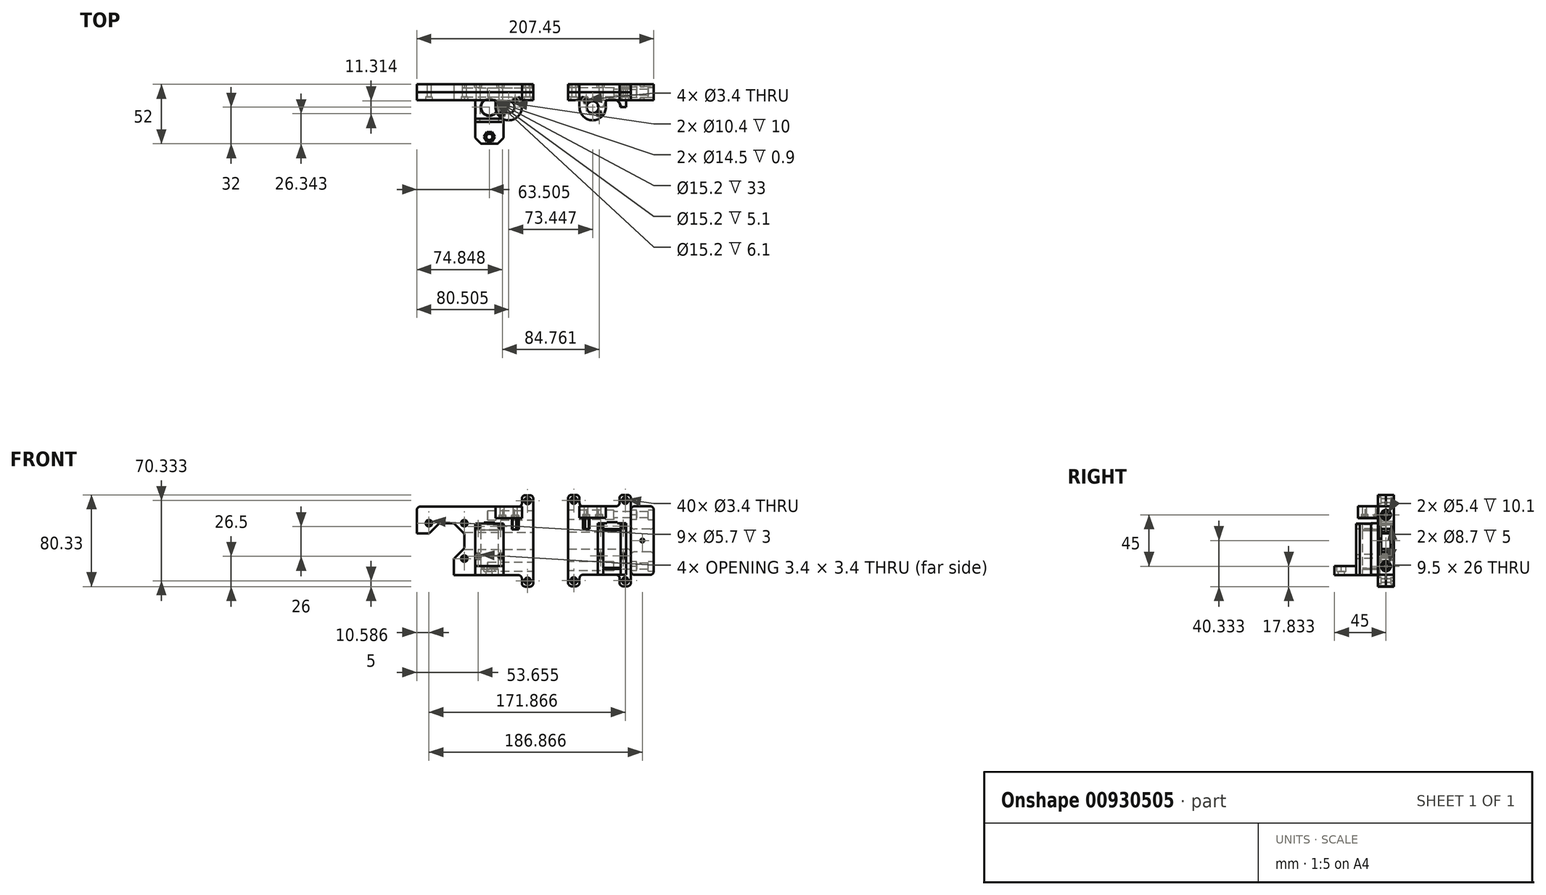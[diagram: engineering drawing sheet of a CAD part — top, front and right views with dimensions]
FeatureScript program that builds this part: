
annotation { "Feature Type Name" : "Feature", "Feature Type Description" : "" }
export const myFeature = defineFeature(function(context is Context, id is Id, definition is map)
    precondition{}
    {
        {
            assignVariable(context, id + "F0", {"name" : "Tolerance", "anyValue" : 0.2 * mm});
        }
        {
            assignVariable(context, id + "F1", {"name" : "RodHoleDepth", "anyValue" : 40 * mm});
        }
        {
            assignVariable(context, id + "F2", {"name" : "M3HeadRecessDepth", "anyValue" : 3 * mm});
        }
        {
            assignVariable(context, id + "F3", {"name" : "M3HexNutDepth", "anyValue" : 2.4 * mm + getVariable(context, 'Tolerance')});
        }
        {
            assignVariable(context, id + "F4", {"name" : "M5HeadRecessDepth", "anyValue" : 5 * mm});
        }
        {
            assignVariable(context, id + "F5", {"name" : "M5HoleDiameter", "anyValue" : 5.2 * mm + getVariable(context, 'Tolerance')});
        }
        {
            assignVariable(context, id + "F6", {"name" : "M5HexNutDepth", "anyValue" : 4.7 * mm + getVariable(context, 'Tolerance')});
        }
        {
            assignVariable(context, id + "F7", {"name" : "FilletRadius", "anyValue" : 3 * mm});
        }
        {
            var Q0;
            Q0=qCreatedBy(makeId("Front.planeOp"),FACE);
            var sketch = newSketch(context, id + "F8", { "sketchPlane" : qUnion([Q0])});
            skLineSegment(sketch, "E0", {"start": v(-115.9, 20) * mm, "end": v(-23.9, 20) * mm});
            skLineSegment(sketch, "E1", {"start": v(-23.9, 20) * mm, "end": v(-23.9, 10) * mm});
            skLineSegment(sketch, "E2", {"start": v(-115.9, 20) * mm, "end": v(-115.9, 80) * mm});
            skLineSegment(sketch, "E3", {"start": v(-115.9, 80) * mm, "end": v(-23.9, 80) * mm});
            skLineSegment(sketch, "E4", {"start": v(-23.9, 80) * mm, "end": v(-23.9, 90) * mm});
            skLineSegment(sketch, "E5", {"start": v(-13.9, 80) * mm, "end": v(-13.9, 20) * mm});
            skLineSegment(sketch, "E6", {"start": v(-13.9, 80) * mm, "end": v(-13.9, 90) * mm});
            skLineSegment(sketch, "E7", {"start": v(-13.9, 20) * mm, "end": v(-13.9, 10) * mm});
            skLineSegment(sketch, "E8", {"start": v(-23.9, 20) * mm, "end": v(-13.9, 20) * mm});
            skLineSegment(sketch, "E9", {"start": v(-23.9, 80) * mm, "end": v(-13.9, 80) * mm});
            skLineSegment(sketch, "E10", {"start": v(-13.9, 90) * mm, "end": v(-23.9, 90) * mm});
            skLineSegment(sketch, "E11", {"start": v(-13.9, 10) * mm, "end": v(-23.9, 10) * mm});
            skSolve(sketch);
        }
        {
            var Q0;
            Q0 = qSketchRegion(id + "F8", true);
            extrude(context, id + "F9", {"entities" : qUnion([Q0]), "oppositeDirection" : true, "depth" : 7 * mm, "offsetDistance" : 25 * mm});
        }
        {
            var Q0;
            Q0 = qSketchRegion(id + "F8", true);
            extrude(context, id + "F10", {"entities" : qUnion([Q0]), "depth" : 7 * mm, "offsetDistance" : 25 * mm});
        }
        {
            var Q0;
            Q0=makeQuery(id+"F10.opExtrude","CAP_FACE",FACE,{"disambiguationData":[OSD([sQuery(id+"F8.wireOp",EDGE,"E0"),sQuery(id+"F8.wireOp",EDGE,"E1"),sQuery(id+"F8.wireOp",EDGE,"4ElTsRrF-d6Ta-Xpu3-N1rJ-FU14qHi0ozwZ"),sQuery(id+"F8.wireOp",EDGE,"7PxteJ0w-hNWy-X14L-V5LG-c6Ao6gPeCcrO"),sQuery(id+"F8.wireOp",EDGE,"Jx2hsfEg-rsGK-g6mN-gGwm-UTiYR1x8r5xO"),sQuery(id+"F8.wireOp",EDGE,"E2"),sQuery(id+"F8.wireOp",EDGE,"E3"),sQuery(id+"F8.wireOp",EDGE,"E4"),sQuery(id+"F8.wireOp",EDGE,"orgWuDI4-4pWB-4aS4-cs57-z0Hx2wF69UBw"),sQuery(id+"F8.wireOp",EDGE,"4i0MoKHX-XmxI-cSmD-P7XZ-JZizBw6dTzRK"),sQuery(id+"F8.wireOp",EDGE,"mOqyP8SL-vEXn-Shjf-BXRA-A4QvbKXMYqA2"),sQuery(id+"F8.wireOp",EDGE,"E5")])],"isStart":false});
            var sketch = newSketch(context, id + "F11", { "sketchPlane" : qUnion([Q0])});
            skCircle(sketch, "E12.cCircle", {"center": v(-89.82, 50) * mm, "radius": 15.5 * mm, "construction": true});
            skLineSegment(sketch, "E12.0", {"start": v(-96.25, 65.5) * mm, "end": v(-83.4, 65.5) * mm});
            skLineSegment(sketch, "E12.1", {"start": v(-83.4, 65.5) * mm, "end": v(-74.32, 56.42) * mm});
            skLineSegment(sketch, "E12.2", {"start": v(-74.32, 56.42) * mm, "end": v(-74.32, 43.58) * mm});
            skLineSegment(sketch, "E12.3", {"start": v(-74.32, 43.58) * mm, "end": v(-83.4, 34.5) * mm});
            skLineSegment(sketch, "E12.7", {"start": v(-105.33, 56.42) * mm, "end": v(-96.25, 65.5) * mm});
            skPoint(sketch, "E12.0.midPoint", {"position": v(-89.82, 65.5) * mm});
            skLineSegment(sketch, "E13", {"start": v(-83.4, 34.5) * mm, "end": v(-83.4, 20) * mm});
            skLineSegment(sketch, "E14", {"start": v(-83.4, 20) * mm, "end": v(-115.9, 20) * mm});
            skLineSegment(sketch, "E15", {"start": v(-105.33, 56.42) * mm, "end": v(-115.9, 56.42) * mm});
            skLineSegment(sketch, "E16", {"start": v(-115.9, 56.42) * mm, "end": v(-115.9, 20) * mm});
            skSolve(sketch);
        }
        {
            var Q0;
            Q0 = qSketchRegion(id + "F11", true);
            extrude(context, id + "F12", {"entities" : qUnion([Q0]), "operationType" : NewBodyOperationType.REMOVE, "oppositeDirection" : true, "depth" : 25 * mm, "offsetDistance" : 25 * mm});
        }
        {
            var Q0;
            Q0=makeQuery(id+"F10.opExtrude","CAP_FACE",FACE,{"disambiguationData":[OSD([sQuery(id+"F8.wireOp",EDGE,"E0"),sQuery(id+"F8.wireOp",EDGE,"E1"),sQuery(id+"F8.wireOp",EDGE,"4ElTsRrF-d6Ta-Xpu3-N1rJ-FU14qHi0ozwZ"),sQuery(id+"F8.wireOp",EDGE,"7PxteJ0w-hNWy-X14L-V5LG-c6Ao6gPeCcrO"),sQuery(id+"F8.wireOp",EDGE,"Jx2hsfEg-rsGK-g6mN-gGwm-UTiYR1x8r5xO"),sQuery(id+"F8.wireOp",EDGE,"E2"),sQuery(id+"F8.wireOp",EDGE,"E3"),sQuery(id+"F8.wireOp",EDGE,"E4"),sQuery(id+"F8.wireOp",EDGE,"orgWuDI4-4pWB-4aS4-cs57-z0Hx2wF69UBw"),sQuery(id+"F8.wireOp",EDGE,"4i0MoKHX-XmxI-cSmD-P7XZ-JZizBw6dTzRK"),sQuery(id+"F8.wireOp",EDGE,"mOqyP8SL-vEXn-Shjf-BXRA-A4QvbKXMYqA2"),sQuery(id+"F8.wireOp",EDGE,"E5")])],"isStart":false});
            var sketch = newSketch(context, id + "F13", { "sketchPlane" : qUnion([Q0])});
            skPoint(sketch, "E17", {"position": v(-74.32, 65.5) * mm});
            skPoint(sketch, "E18", {"position": v(-74.32, 34.5) * mm});
            skCircle(sketch, "E19", {"center": v(-105.32, 65.5) * mm, "radius": 1.7 * mm});
            skCircle(sketch, "E20", {"center": v(-74.32, 65.5) * mm, "radius": 1.7 * mm});
            skCircle(sketch, "E21", {"center": v(-74.32, 34.5) * mm, "radius": 1.7 * mm});
            skCircle(sketch, "E22", {"center": v(-18.9, 85) * mm, "radius": 1.7 * mm});
            skPoint(sketch, "E22.centerSnap0", {"position": v(-23.9, 85) * mm});
            skPoint(sketch, "E22.centerSnap1", {"position": v(-18.9, 90) * mm});
            skCircle(sketch, "E23", {"center": v(-18.9, 15) * mm, "radius": 1.7 * mm});
            skPoint(sketch, "E23.centerSnap0", {"position": v(-18.9, 10) * mm});
            skPoint(sketch, "E23.centerSnap1", {"position": v(-23.9, 15) * mm});
            skSolve(sketch);
        }
        {
            var Q0;
            Q0 = qSketchRegion(id + "F13", true);
            extrude(context, id + "F14", {"entities" : qUnion([Q0]), "operationType" : NewBodyOperationType.REMOVE, "oppositeDirection" : true, "depth" : 25 * mm, "offsetDistance" : 25 * mm});
        }
        {
            var Q0;
            Q0=makeQuery(id+"F10.opExtrude","SWEPT_FACE",FACE,{"disambiguationData":[OSD([sQuery(id+"F8.wireOp",EDGE,"E5")])]});
            var sketch = newSketch(context, id + "F15", { "sketchPlane" : qUnion([Q0])});
            skLineSegment(sketch, "E24.bottom", {"start": v(-4, 42.5) * mm, "end": v(4, 42.5) * mm});
            skLineSegment(sketch, "E24.top", {"start": v(-4, 57.5) * mm, "end": v(4, 57.5) * mm});
            skLineSegment(sketch, "E24.left", {"start": v(-4, 42.5) * mm, "end": v(-4, 57.5) * mm});
            skLineSegment(sketch, "E24.right", {"start": v(4, 42.5) * mm, "end": v(4, 57.5) * mm});
            skSolve(sketch);
        }
        {
            var Q0;
            Q0 = qSketchRegion(id + "F15", true);
            extrude(context, id + "F16", {"entities" : qUnion([Q0]), "operationType" : NewBodyOperationType.REMOVE, "oppositeDirection" : true, "depth" : 65 * mm, "offsetDistance" : 25 * mm});
        }
        {
            var Q0;
            Q0=makeQuery(id+"F9.opExtrude","SWEPT_FACE",FACE,{"disambiguationData":[OSD([sQuery(id+"F8.wireOp",EDGE,"E5")])]});
            var sketch = newSketch(context, id + "F17", { "sketchPlane" : qUnion([Q0])});
            skCircle(sketch, "E25", {"center": v(0, 72.5) * mm, "radius": 4.1 * mm});
            skCircle(sketch, "E26", {"center": v(0, 27.5) * mm, "radius": 4.1 * mm});
            skSolve(sketch);
        }
        {
            var Q0;
            Q0 = qSketchRegion(id + "F17", true);
            extrude(context, id + "F18", {"entities" : qUnion([Q0]), "operationType" : NewBodyOperationType.REMOVE, "oppositeDirection" : true, "depth" : (getVariable(context, 'RodHoleDepth')), "offsetDistance" : 25 * mm});
        }
        {
            var Q0;
            Q0=makeQuery(id+"F10.opExtrude","SWEPT_FACE",FACE,{"disambiguationData":[OSD([sQuery(id+"F8.wireOp",EDGE,"E3")])]});
            var sketch = newSketch(context, id + "F19", { "sketchPlane" : qUnion([Q0])});
            skPoint(sketch, "E27", {"position": v(-46.9, -7) * mm});
            skPoint(sketch, "E28", {"position": v(-23.9, -7) * mm});
            skPoint(sketch, "E29", {"position": v(-35.4, -7) * mm});
            skPoint(sketch, "E30", {"position": v(-35.4, -13) * mm});
            skCircle(sketch, "E31", {"center": v(-35.4, -13) * mm, "radius": 5.2 * mm});
            skPoint(sketch, "E32", {"position": v(-35.4, -24.5) * mm});
            skLineSegment(sketch, "E33", {"start": v(-46.9, -7) * mm, "end": v(-23.9, -7) * mm});
            skArc(sketch, "E34", {"start": v(-35.4, -24.5) * mm, "mid": v(-27.27, -21.13) * mm, "end": v(-23.9, -13) * mm});
            skArc(sketch, "E35", {"start": v(-35.4, -24.5) * mm, "mid": v(-43.54, -21.13) * mm, "end": v(-46.9, -13) * mm});
            skLineSegment(sketch, "E36", {"start": v(-23.9, -7) * mm, "end": v(-23.9, -13) * mm});
            skLineSegment(sketch, "E37", {"start": v(-46.9, -7) * mm, "end": v(-46.9, -13) * mm});
            skSolve(sketch);
        }
        {
            var Q0;
            Q0 = qSketchRegion(id + "F19", true);
            extrude(context, id + "F20", {"entities" : qUnion([Q0]), "operationType" : NewBodyOperationType.ADD, "oppositeDirection" : true, "depth" : 10 * mm, "offsetDistance" : 25 * mm});
        }
        {
            var Q0;
            Q0=makeQuery(id+"F20.boolean.opBoolean","MERGE",FACE,{"derivedFrom":[makeQuery(id+"F10.opExtrude","SWEPT_FACE",FACE,{"disambiguationData":[OSD([sQuery(id+"F8.wireOp",EDGE,"E3")])]}),makeQuery(id+"F20.opExtrude","CAP_FACE",FACE,{"disambiguationData":[OSD([sQuery(id+"F19.wireOp",EDGE,"E31"),sQuery(id+"F19.wireOp",EDGE,"E33"),sQuery(id+"F19.wireOp",EDGE,"E34"),sQuery(id+"F19.wireOp",EDGE,"E35"),sQuery(id+"F19.wireOp",EDGE,"E36"),sQuery(id+"F19.wireOp",EDGE,"E37")])],"isStart":true})]});
            var sketch = newSketch(context, id + "F21", { "sketchPlane" : qUnion([Q0])});
            skPoint(sketch, "E38", {"position": v(-35.4, -13) * mm});
            skLineSegment(sketch, "E39", {"start": v(-35.4, -13) * mm, "end": v(-35.4, -5) * mm});
            skLineSegment(sketch, "E40", {"start": v(-35.4, -13) * mm, "end": v(-29.75, -7.34) * mm});
            skLineSegment(sketch, "E41", {"start": v(-35.4, -13) * mm, "end": v(-29.75, -18.66) * mm});
            skLineSegment(sketch, "E42", {"start": v(-35.4, -13) * mm, "end": v(-41.06, -18.66) * mm});
            skLineSegment(sketch, "E43", {"start": v(-35.4, -13) * mm, "end": v(-41.06, -7.34) * mm});
            skCircle(sketch, "E44", {"center": v(-29.75, -7.34) * mm, "radius": 1.7 * mm});
            skCircle(sketch, "E45", {"center": v(-41.06, -18.66) * mm, "radius": 1.7 * mm});
            skSolve(sketch);
        }
        {
            var Q0;
            Q0 = qSketchRegion(id + "F21", true);
            extrude(context, id + "F22", {"entities" : qUnion([Q0]), "operationType" : NewBodyOperationType.REMOVE, "oppositeDirection" : true, "depth" : 12.5 * mm, "offsetDistance" : 25 * mm});
        }
        {
            var Q0;
            Q0=makeQuery(id+"F20.opExtrude","CAP_FACE",FACE,{"disambiguationData":[OSD([sQuery(id+"F19.wireOp",EDGE,"E31"),sQuery(id+"F19.wireOp",EDGE,"E33"),sQuery(id+"F19.wireOp",EDGE,"E34"),sQuery(id+"F19.wireOp",EDGE,"E35"),sQuery(id+"F19.wireOp",EDGE,"E36"),sQuery(id+"F19.wireOp",EDGE,"E37")])],"isStart":false});
            var sketch = newSketch(context, id + "F23", { "sketchPlane" : qUnion([Q0])});
            skPoint(sketch, "E46", {"position": v(-35.4, 13) * mm});
            skPoint(sketch, "E47", {"position": v(-41.06, 18.66) * mm});
            skPoint(sketch, "E48.positionSnap0", {"position": v(-29.75, 9.04) * mm});
            skLineSegment(sketch, "E49", {"start": v(-41.06, 18.66) * mm, "end": v(-35.4, 13) * mm});
            skLineSegment(sketch, "E50", {"start": v(-35.4, 13) * mm, "end": v(-29.75, 7.34) * mm});
            skCircle(sketch, "E51.cCircle", {"center": v(-41.06, 18.66) * mm, "radius": 2.8 * mm, "construction": true});
            skLineSegment(sketch, "E51.0", {"start": v(-37.94, 17.82) * mm, "end": v(-40.23, 15.53) * mm});
            skLineSegment(sketch, "E51.1", {"start": v(-40.23, 15.53) * mm, "end": v(-43.35, 16.37) * mm});
            skLineSegment(sketch, "E51.2", {"start": v(-43.35, 16.37) * mm, "end": v(-44.19, 19.5) * mm});
            skLineSegment(sketch, "E51.3", {"start": v(-44.19, 19.5) * mm, "end": v(-41.9, 21.78) * mm});
            skLineSegment(sketch, "E51.4", {"start": v(-41.9, 21.78) * mm, "end": v(-38.78, 20.94) * mm});
            skLineSegment(sketch, "E51.5", {"start": v(-38.78, 20.94) * mm, "end": v(-37.94, 17.82) * mm});
            skPoint(sketch, "E51.0.midPoint", {"position": v(-39.08, 16.68) * mm});
            skCircle(sketch, "E52.cCircle", {"center": v(-29.75, 7.34) * mm, "radius": 2.8 * mm, "construction": true});
            skLineSegment(sketch, "E52.0", {"start": v(-32.87, 8.18) * mm, "end": v(-30.59, 10.47) * mm});
            skLineSegment(sketch, "E52.1", {"start": v(-30.59, 10.47) * mm, "end": v(-27.46, 9.63) * mm});
            skLineSegment(sketch, "E52.2", {"start": v(-27.46, 9.63) * mm, "end": v(-26.63, 6.5) * mm});
            skLineSegment(sketch, "E52.3", {"start": v(-26.63, 6.5) * mm, "end": v(-28.91, 4.22) * mm});
            skLineSegment(sketch, "E52.4", {"start": v(-28.91, 4.22) * mm, "end": v(-32.03, 5.06) * mm});
            skLineSegment(sketch, "E52.5", {"start": v(-32.03, 5.06) * mm, "end": v(-32.87, 8.18) * mm});
            skPoint(sketch, "E52.0.midPoint", {"position": v(-31.73, 9.32) * mm});
            skLineSegment(sketch, "E53", {"start": v(-40.23, 15.53) * mm, "end": v(-39.26, 15.28) * mm});
            skLineSegment(sketch, "E54", {"start": v(-37.94, 17.82) * mm, "end": v(-37.68, 16.85) * mm});
            skLineSegment(sketch, "E55", {"start": v(-39.26, 15.28) * mm, "end": v(-37.68, 16.85) * mm});
            skLineSegment(sketch, "E56", {"start": v(-32.87, 8.18) * mm, "end": v(-33.13, 9.15) * mm});
            skLineSegment(sketch, "E57", {"start": v(-30.59, 10.47) * mm, "end": v(-31.55, 10.72) * mm});
            skLineSegment(sketch, "E58", {"start": v(-33.13, 9.15) * mm, "end": v(-31.55, 10.72) * mm});
            skSolve(sketch);
        }
        {
            var Q0;
            Q0 = qSketchRegion(id + "F23", true);
            extrude(context, id + "F24", {"entities" : qUnion([Q0]), "operationType" : NewBodyOperationType.REMOVE, "oppositeDirection" : true, "depth" : (getVariable(context, 'M3HexNutDepth')), "offsetDistance" : 25 * mm});
        }
        {
            var Q0;
            Q0 = qSketchRegion(id + "F23", true);
            extrude(context, id + "F25", {"entities" : qUnion([Q0]), "operationType" : NewBodyOperationType.REMOVE, "depth" : 10 * mm, "offsetDistance" : 25 * mm});
        }
        {
            var Q0;
            Q0=makeQuery(id+"F10.opExtrude","SWEPT_FACE",FACE,{"disambiguationData":[OSD([sQuery(id+"F8.wireOp",EDGE,"E0")])]});
            var sketch = newSketch(context, id + "F26", { "sketchPlane" : qUnion([Q0])});
            skPoint(sketch, "E59", {"position": v(-35.4, 7) * mm});
            skPoint(sketch, "E60", {"position": v(-52.4, 13) * mm});
            skArc(sketch, "E61", {"start": v(-44.8, 13) * mm, "mid": v(-52.4, 5.4) * mm, "end": v(-60, 13) * mm});
            skArc(sketch, "E62", {"start": v(-48.4, 13) * mm, "mid": v(-52.4, 9) * mm, "end": v(-56.4, 13) * mm});
            skLineSegment(sketch, "E63", {"start": v(-56.4, 13) * mm, "end": v(-60, 13) * mm});
            skLineSegment(sketch, "E64", {"start": v(-48.4, 13) * mm, "end": v(-44.8, 13) * mm});
            skPoint(sketch, "E65", {"position": v(-35.4, 13) * mm});
            skSolve(sketch);
        }
        {
            var Q0;
            Q0 = qSketchRegion(id + "F26", true);
            extrude(context, id + "F27", {"entities" : qUnion([Q0]), "operationType" : NewBodyOperationType.REMOVE, "oppositeDirection" : true, "depth" : 46 * mm, "offsetDistance" : 25 * mm});
        }
        {
            var Q0;
            Q0=makeQuery(id+"F10.opExtrude","SWEPT_FACE",FACE,{"disambiguationData":[OSD([sQuery(id+"F8.wireOp",EDGE,"E0")])]});
            var sketch = newSketch(context, id + "F28", { "sketchPlane" : qUnion([Q0])});
            skPoint(sketch, "E66", {"position": v(-52.4, 13) * mm});
            skArc(sketch, "E67", {"start": v(-60, 13) * mm, "mid": v(-52.4, 5.4) * mm, "end": v(-44.8, 13) * mm});
            skLineSegment(sketch, "E68", {"start": v(-44.8, 13) * mm, "end": v(-40.06, 13) * mm});
            skLineSegment(sketch, "E69", {"start": v(-60, 13) * mm, "end": v(-64.76, 13) * mm});
            skLineSegment(sketch, "E70", {"start": v(-40.06, 13) * mm, "end": v(-40.06, 7) * mm});
            skLineSegment(sketch, "E71", {"start": v(-40.06, 7) * mm, "end": v(-47.74, 7) * mm});
            skLineSegment(sketch, "E72", {"start": v(-64.76, 13) * mm, "end": v(-64.76, 7) * mm});
            skLineSegment(sketch, "E73", {"start": v(-64.76, 7) * mm, "end": v(-57.07, 7) * mm});
            skSolve(sketch);
        }
        {
            var Q0;
            Q0 = qSketchRegion(id + "F28", true);
            extrude(context, id + "F29", {"entities" : qUnion([Q0]), "operationType" : NewBodyOperationType.ADD, "oppositeDirection" : true, "depth" : (5 * mm + getVariable(context, 'Tolerance') / 2), "offsetDistance" : 25 * mm});
        }
        {
            var Q0;
            Q0=makeQuery(id+"F29.opExtrude","CAP_FACE",FACE,{"disambiguationData":[OSD([sQuery(id+"F28.wireOp",EDGE,"E67"),sQuery(id+"F28.wireOp",EDGE,"E68"),sQuery(id+"F28.wireOp",EDGE,"E70"),sQuery(id+"F28.wireOp",EDGE,"E71")])],"isStart":false});
            var sketch = newSketch(context, id + "F30", { "sketchPlane" : qUnion([Q0])});
            skPoint(sketch, "E74", {"position": v(-52.4, -13) * mm});
            skArc(sketch, "E75", {"start": v(-45.16, -13) * mm, "mid": v(-52.4, -5.75) * mm, "end": v(-59.66, -13) * mm});
            skLineSegment(sketch, "E76", {"start": v(-45.16, -13) * mm, "end": v(-40.06, -13) * mm});
            skLineSegment(sketch, "E77", {"start": v(-40.06, -13) * mm, "end": v(-40.06, -5) * mm});
            skLineSegment(sketch, "E78", {"start": v(-59.66, -13) * mm, "end": v(-64.76, -13) * mm});
            skLineSegment(sketch, "E79", {"start": v(-64.76, -13) * mm, "end": v(-64.76, -5) * mm});
            skLineSegment(sketch, "E80", {"start": v(-64.76, -5) * mm, "end": v(-40.06, -5) * mm});
            skSolve(sketch);
        }
        {
            var Q0;
            Q0 = qSketchRegion(id + "F30", true);
            extrude(context, id + "F31", {"entities" : qUnion([Q0]), "operationType" : NewBodyOperationType.ADD, "depth" : 1.1 * mm - getVariable(context, 'Tolerance'), "offsetDistance" : 25 * mm});
        }
        {
            var Q0;
            Q0=makeQuery(id+"F31.opExtrude","CAP_FACE",FACE,{"disambiguationData":[OSD([sQuery(id+"F30.wireOp",EDGE,"E75"),sQuery(id+"F30.wireOp",EDGE,"xVCJ5Ixd-oV9c-nEpF-QwK2-FCStSbNz6csr"),sQuery(id+"F30.wireOp",EDGE,"KKsrvb3y-Tanb-XRHW-Xvde-AmVJSpIleMcL"),sQuery(id+"F30.wireOp",EDGE,"jJWCP0GL-qmZ0-jQ3C-Ld0P-dRRUBaJsqygn"),sQuery(id+"F30.wireOp",EDGE,"l5prBngy-kXb7-NS8M-DBdE-vMuQnj67Dzb8"),sQuery(id+"F30.wireOp",EDGE,"qzUSBdcP-XdCP-zqGN-MzMA-phhTVpw7iq0O")])],"isStart":false});
            var sketch = newSketch(context, id + "F32", { "sketchPlane" : qUnion([Q0])});
            skPoint(sketch, "E81", {"position": v(-52.4, -13) * mm});
            skArc(sketch, "E82", {"start": v(-44.8, -13) * mm, "mid": v(-52.4, -5.4) * mm, "end": v(-60, -13) * mm});
            skLineSegment(sketch, "E83", {"start": v(-60, -13) * mm, "end": v(-64.76, -13) * mm});
            skLineSegment(sketch, "E84", {"start": v(-64.76, -13) * mm, "end": v(-64.76, -5) * mm});
            skLineSegment(sketch, "E85", {"start": v(-44.8, -13) * mm, "end": v(-40.06, -13) * mm});
            skLineSegment(sketch, "E86", {"start": v(-40.06, -13) * mm, "end": v(-40.06, -5) * mm});
            skLineSegment(sketch, "E87", {"start": v(-64.76, -5) * mm, "end": v(-40.06, -5) * mm});
            skSolve(sketch);
        }
        {
            var Q0;
            Q0 = qSketchRegion(id + "F32", true);
            extrude(context, id + "F33", {"entities" : qUnion([Q0]), "operationType" : NewBodyOperationType.ADD, "depth" : 32.8 * mm + getVariable(context, 'Tolerance'), "offsetDistance" : 25 * mm});
        }
        {
            var Q0;
            {var subQ0=sQuery(id+"F32.wireOp",EDGE,"u7j6INuo-gqj2-xr2Y-Kvyz-7sy1viPy3Nbp");var subQ1=sQuery(id+"F32.wireOp",EDGE,"E82");var subQ3=sQuery(id+"F28.wireOp",EDGE,"E69");var subQ4=sQuery(id+"F32.wireOp",EDGE,"uuo2rrgI-b8Mf-HUeX-D92I-OpvW8boPGIY9");Q0=makeQuery(id+"F33.boolean.opBoolean","SPLIT",FACE,{"disambiguationData":[TD([makeQuery(id+"F29.opExtrude","SWEPT_FACE",FACE,{"disambiguationData":[OSD([subQ3])]})])],"derivedFrom":makeQuery(id+"F33.opExtrude","CAP_FACE",FACE,{"disambiguationData":[OSD([subQ1,subQ0,sQuery(id+"F32.wireOp",EDGE,"ZIB3AkM0-OxwD-h3Ax-mLtj-ZQacNZoiAByL"),sQuery(id+"F32.wireOp",EDGE,"DisRxEdu-4dno-EZQz-xngY-1mmXhpX3mB9u"),subQ4,sQuery(id+"F32.wireOp",EDGE,"J3FYGhw3-x3kB-kLge-yOmn-sRuC37IefDrh")])],"isStart":false})});}
            var sketch = newSketch(context, id + "F34", { "sketchPlane" : qUnion([Q0])});
            skPoint(sketch, "E88", {"position": v(-52.4, -13) * mm});
            skArc(sketch, "E89", {"start": v(-45.16, -13) * mm, "mid": v(-52.4, -5.75) * mm, "end": v(-59.66, -13) * mm});
            skLineSegment(sketch, "E90", {"start": v(-59.66, -13) * mm, "end": v(-64.76, -13) * mm});
            skLineSegment(sketch, "E91", {"start": v(-45.16, -13) * mm, "end": v(-40.06, -13) * mm});
            skLineSegment(sketch, "E92", {"start": v(-40.06, -13) * mm, "end": v(-40.06, -5) * mm});
            skLineSegment(sketch, "E93", {"start": v(-64.76, -13) * mm, "end": v(-64.76, -5) * mm});
            skLineSegment(sketch, "E94", {"start": v(-64.76, -5) * mm, "end": v(-40.06, -5) * mm});
            skSolve(sketch);
        }
        {
            var Q0;
            Q0 = qSketchRegion(id + "F34", true);
            extrude(context, id + "F35", {"entities" : qUnion([Q0]), "operationType" : NewBodyOperationType.ADD, "depth" : 1.1 * mm - getVariable(context, 'Tolerance'), "offsetDistance" : 25 * mm});
        }
        {
            var Q0;
            Q0=makeQuery(id+"F35.opExtrude","CAP_FACE",FACE,{"disambiguationData":[OSD([sQuery(id+"F34.wireOp",EDGE,"E89"),sQuery(id+"F34.wireOp",EDGE,"GdwB4Kny-1C7h-vXFo-lqtw-lYCse3TfWah3"),sQuery(id+"F34.wireOp",EDGE,"UIoDu40C-p5wn-kfFw-dchT-OTPBX3CLgIoY"),sQuery(id+"F34.wireOp",EDGE,"nKK0WJDT-j9Y7-Eu8t-1ZP1-kCxPYY3NenT9"),sQuery(id+"F34.wireOp",EDGE,"1FnQ6s0P-5r0c-BRcY-ZU3t-i9w6pcUyLMfj"),sQuery(id+"F34.wireOp",EDGE,"748WQctB-3RJW-Xf6T-p68E-eUlEy1FFqQs4")])],"isStart":false});
            var sketch = newSketch(context, id + "F36", { "sketchPlane" : qUnion([Q0])});
            skPoint(sketch, "E95", {"position": v(-52.4, -13) * mm});
            skArc(sketch, "E96", {"start": v(-44.8, -13) * mm, "mid": v(-52.4, -5.4) * mm, "end": v(-60, -13) * mm});
            skLineSegment(sketch, "E97", {"start": v(-44.8, -13) * mm, "end": v(-40.06, -13) * mm});
            skLineSegment(sketch, "E98", {"start": v(-40.06, -13) * mm, "end": v(-40.06, -5) * mm});
            skLineSegment(sketch, "E99", {"start": v(-60, -13) * mm, "end": v(-64.76, -13) * mm});
            skLineSegment(sketch, "E100", {"start": v(-64.76, -13) * mm, "end": v(-64.76, -5) * mm});
            skLineSegment(sketch, "E101", {"start": v(-64.76, -5) * mm, "end": v(-40.06, -5) * mm});
            skSolve(sketch);
        }
        {
            var Q0;
            Q0 = qSketchRegion(id + "F36", true);
            extrude(context, id + "F37", {"entities" : qUnion([Q0]), "operationType" : NewBodyOperationType.ADD, "depth" : 5 * mm + (getVariable(context, 'Tolerance') / 2), "offsetDistance" : 25 * mm});
        }
        {
            var Q0;
            Q0=makeQuery(id+"F37.boolean.opBoolean","MERGE",FACE,{"derivedFrom":[makeQuery(id+"F35.boolean.opBoolean","MERGE",FACE,{"derivedFrom":[makeQuery(id+"F33.boolean.opBoolean","MERGE",FACE,{"derivedFrom":[makeQuery(id+"F31.boolean.opBoolean","MERGE",FACE,{"derivedFrom":[makeQuery(id+"F29.opExtrude","SWEPT_FACE",FACE,{"disambiguationData":[OSD([sQuery(id+"F28.wireOp",EDGE,"E69")])]}),makeQuery(id+"F31.opExtrude","SWEPT_FACE",FACE,{"disambiguationData":[OSD([sQuery(id+"F30.wireOp",EDGE,"xVCJ5Ixd-oV9c-nEpF-QwK2-FCStSbNz6csr")])]})]}),makeQuery(id+"F33.opExtrude","SWEPT_FACE",FACE,{"disambiguationData":[OSD([sQuery(id+"F32.wireOp",EDGE,"u7j6INuo-gqj2-xr2Y-Kvyz-7sy1viPy3Nbp")])]})]}),makeQuery(id+"F35.opExtrude","SWEPT_FACE",FACE,{"disambiguationData":[OSD([sQuery(id+"F34.wireOp",EDGE,"UIoDu40C-p5wn-kfFw-dchT-OTPBX3CLgIoY")])]})]}),makeQuery(id+"F37.opExtrude","SWEPT_FACE",FACE,{"disambiguationData":[OSD([sQuery(id+"F36.wireOp",EDGE,"6wegHLb0-SrSl-BNs0-chY1-SGuGLHtS43J8")])]})]});
            var sketch = newSketch(context, id + "F38", { "sketchPlane" : qUnion([Q0])});
            skPoint(sketch, "E102", {"position": v(-62.26, 62.5) * mm});
            skCircle(sketch, "E103", {"center": v(-62.26, 62.5) * mm, "radius": 1.7 * mm});
            skPoint(sketch, "E104", {"position": v(-62.26, 36.5) * mm});
            skPoint(sketch, "E105", {"position": v(-42.56, 62.5) * mm});
            skCircle(sketch, "E106", {"center": v(-42.56, 62.5) * mm, "radius": 1.7 * mm});
            skCircle(sketch, "E107", {"center": v(-62.26, 36.5) * mm, "radius": 1.7 * mm});
            skPoint(sketch, "E108", {"position": v(-42.56, 36.5) * mm});
            skCircle(sketch, "E109", {"center": v(-42.56, 36.5) * mm, "radius": 1.7 * mm});
            skSolve(sketch);
        }
        {
            var Q0;
            Q0 = qSketchRegion(id + "F38", true);
            extrude(context, id + "F39", {"entities" : qUnion([Q0]), "operationType" : NewBodyOperationType.REMOVE, "oppositeDirection" : true, "depth" : 20 * mm, "offsetDistance" : 25 * mm});
        }
        {
            var Q0;
            Q0=makeQuery(id+"F9.opExtrude","CAP_FACE",FACE,{"disambiguationData":[OSD([sQuery(id+"F8.wireOp",EDGE,"E0"),sQuery(id+"F8.wireOp",EDGE,"E1"),sQuery(id+"F8.wireOp",EDGE,"4ElTsRrF-d6Ta-Xpu3-N1rJ-FU14qHi0ozwZ"),sQuery(id+"F8.wireOp",EDGE,"7PxteJ0w-hNWy-X14L-V5LG-c6Ao6gPeCcrO"),sQuery(id+"F8.wireOp",EDGE,"Jx2hsfEg-rsGK-g6mN-gGwm-UTiYR1x8r5xO"),sQuery(id+"F8.wireOp",EDGE,"E2"),sQuery(id+"F8.wireOp",EDGE,"E3"),sQuery(id+"F8.wireOp",EDGE,"E4"),sQuery(id+"F8.wireOp",EDGE,"orgWuDI4-4pWB-4aS4-cs57-z0Hx2wF69UBw"),sQuery(id+"F8.wireOp",EDGE,"4i0MoKHX-XmxI-cSmD-P7XZ-JZizBw6dTzRK"),sQuery(id+"F8.wireOp",EDGE,"mOqyP8SL-vEXn-Shjf-BXRA-A4QvbKXMYqA2"),sQuery(id+"F8.wireOp",EDGE,"E5")])],"isStart":false});
            var sketch = newSketch(context, id + "F40", { "sketchPlane" : qUnion([Q0])});
            skCircle(sketch, "E110.cCircle", {"center": v(18.9, 85) * mm, "radius": 2.8 * mm, "construction": true});
            skLineSegment(sketch, "E110.0", {"start": v(17.29, 87.8) * mm, "end": v(20.52, 87.8) * mm});
            skLineSegment(sketch, "E110.1", {"start": v(20.52, 87.8) * mm, "end": v(22.14, 85) * mm});
            skLineSegment(sketch, "E110.2", {"start": v(22.14, 85) * mm, "end": v(20.52, 82.2) * mm});
            skLineSegment(sketch, "E110.3", {"start": v(20.52, 82.2) * mm, "end": v(17.29, 82.2) * mm});
            skLineSegment(sketch, "E110.4", {"start": v(17.29, 82.2) * mm, "end": v(15.67, 85) * mm});
            skLineSegment(sketch, "E110.5", {"start": v(15.67, 85) * mm, "end": v(17.29, 87.8) * mm});
            skPoint(sketch, "E110.0.midPoint", {"position": v(18.9, 87.8) * mm});
            skCircle(sketch, "E111.cCircle", {"center": v(18.9, 15) * mm, "radius": 2.8 * mm, "construction": true});
            skLineSegment(sketch, "E111.0", {"start": v(17.34, 17.83) * mm, "end": v(20.57, 17.77) * mm});
            skLineSegment(sketch, "E111.1", {"start": v(20.57, 17.77) * mm, "end": v(22.14, 14.95) * mm});
            skLineSegment(sketch, "E111.2", {"start": v(22.14, 14.95) * mm, "end": v(20.47, 12.17) * mm});
            skLineSegment(sketch, "E111.3", {"start": v(20.47, 12.17) * mm, "end": v(17.24, 12.23) * mm});
            skLineSegment(sketch, "E111.4", {"start": v(17.24, 12.23) * mm, "end": v(15.67, 15.05) * mm});
            skLineSegment(sketch, "E111.5", {"start": v(15.67, 15.05) * mm, "end": v(17.34, 17.83) * mm});
            skPoint(sketch, "E111.0.midPoint", {"position": v(18.95, 17.8) * mm});
            skCircle(sketch, "E112.cCircle", {"center": v(42.56, 62.5) * mm, "radius": 2.8 * mm, "construction": true});
            skLineSegment(sketch, "E112.0", {"start": v(40.94, 65.3) * mm, "end": v(44.17, 65.3) * mm});
            skLineSegment(sketch, "E112.1", {"start": v(44.17, 65.3) * mm, "end": v(45.79, 62.5) * mm});
            skLineSegment(sketch, "E112.2", {"start": v(45.79, 62.5) * mm, "end": v(44.17, 59.7) * mm});
            skLineSegment(sketch, "E112.3", {"start": v(44.17, 59.7) * mm, "end": v(40.94, 59.7) * mm});
            skLineSegment(sketch, "E112.4", {"start": v(40.94, 59.7) * mm, "end": v(39.32, 62.5) * mm});
            skLineSegment(sketch, "E112.5", {"start": v(39.32, 62.5) * mm, "end": v(40.94, 65.3) * mm});
            skPoint(sketch, "E112.0.midPoint", {"position": v(42.56, 65.3) * mm});
            skCircle(sketch, "E113.cCircle", {"center": v(62.26, 62.5) * mm, "radius": 2.8 * mm, "construction": true});
            skLineSegment(sketch, "E113.0", {"start": v(60.64, 65.3) * mm, "end": v(63.87, 65.3) * mm});
            skLineSegment(sketch, "E113.1", {"start": v(63.87, 65.3) * mm, "end": v(65.49, 62.5) * mm});
            skLineSegment(sketch, "E113.2", {"start": v(65.49, 62.5) * mm, "end": v(63.87, 59.7) * mm});
            skLineSegment(sketch, "E113.3", {"start": v(63.87, 59.7) * mm, "end": v(60.64, 59.7) * mm});
            skLineSegment(sketch, "E113.4", {"start": v(60.64, 59.7) * mm, "end": v(59.02, 62.5) * mm});
            skLineSegment(sketch, "E113.5", {"start": v(59.02, 62.5) * mm, "end": v(60.64, 65.3) * mm});
            skPoint(sketch, "E113.0.midPoint", {"position": v(62.26, 65.3) * mm});
            skCircle(sketch, "E114.cCircle", {"center": v(42.56, 36.5) * mm, "radius": 2.8 * mm, "construction": true});
            skLineSegment(sketch, "E114.0", {"start": v(40.94, 39.3) * mm, "end": v(44.17, 39.3) * mm});
            skLineSegment(sketch, "E114.1", {"start": v(44.17, 39.3) * mm, "end": v(45.79, 36.5) * mm});
            skLineSegment(sketch, "E114.2", {"start": v(45.79, 36.5) * mm, "end": v(44.17, 33.7) * mm});
            skLineSegment(sketch, "E114.3", {"start": v(44.17, 33.7) * mm, "end": v(40.94, 33.7) * mm});
            skLineSegment(sketch, "E114.4", {"start": v(40.94, 33.7) * mm, "end": v(39.32, 36.5) * mm});
            skLineSegment(sketch, "E114.5", {"start": v(39.32, 36.5) * mm, "end": v(40.94, 39.3) * mm});
            skPoint(sketch, "E114.0.midPoint", {"position": v(42.56, 39.3) * mm});
            skCircle(sketch, "E115.cCircle", {"center": v(62.26, 36.5) * mm, "radius": 2.8 * mm, "construction": true});
            skLineSegment(sketch, "E115.0", {"start": v(60.64, 39.3) * mm, "end": v(63.87, 39.3) * mm});
            skLineSegment(sketch, "E115.1", {"start": v(63.87, 39.3) * mm, "end": v(65.49, 36.5) * mm});
            skLineSegment(sketch, "E115.2", {"start": v(65.49, 36.5) * mm, "end": v(63.87, 33.7) * mm});
            skLineSegment(sketch, "E115.3", {"start": v(63.87, 33.7) * mm, "end": v(60.64, 33.7) * mm});
            skLineSegment(sketch, "E115.4", {"start": v(60.64, 33.7) * mm, "end": v(59.02, 36.5) * mm});
            skLineSegment(sketch, "E115.5", {"start": v(59.02, 36.5) * mm, "end": v(60.64, 39.3) * mm});
            skPoint(sketch, "E115.0.midPoint", {"position": v(62.26, 39.3) * mm});
            skSolve(sketch);
        }
        {
            var Q0;
            Q0 = qSketchRegion(id + "F40", true);
            extrude(context, id + "F41", {"entities" : qUnion([Q0]), "operationType" : NewBodyOperationType.REMOVE, "oppositeDirection" : true, "depth" : getVariable(context, 'M3HexNutDepth'), "offsetDistance" : 25 * mm});
        }
        {
            var Q0;
            {var subQ0=sQuery(id+"F8.wireOp",EDGE,"E5");var subQ1=sQuery(id+"F8.wireOp",EDGE,"mOqyP8SL-vEXn-Shjf-BXRA-A4QvbKXMYqA2");var subQ2=sQuery(id+"F8.wireOp",EDGE,"4i0MoKHX-XmxI-cSmD-P7XZ-JZizBw6dTzRK");var subQ3=sQuery(id+"F8.wireOp",EDGE,"orgWuDI4-4pWB-4aS4-cs57-z0Hx2wF69UBw");var subQ4=sQuery(id+"F8.wireOp",EDGE,"E4");var subQ5=sQuery(id+"F8.wireOp",EDGE,"E3");var subQ6=sQuery(id+"F8.wireOp",EDGE,"E2");var subQ7=sQuery(id+"F8.wireOp",EDGE,"Jx2hsfEg-rsGK-g6mN-gGwm-UTiYR1x8r5xO");var subQ8=sQuery(id+"F8.wireOp",EDGE,"7PxteJ0w-hNWy-X14L-V5LG-c6Ao6gPeCcrO");var subQ9=sQuery(id+"F8.wireOp",EDGE,"4ElTsRrF-d6Ta-Xpu3-N1rJ-FU14qHi0ozwZ");var subQ10=sQuery(id+"F8.wireOp",EDGE,"E1");var subQ11=sQuery(id+"F8.wireOp",EDGE,"E0");var subQ12=sQuery(id+"F11.wireOp",EDGE,"E13");var subQ13=sQuery(id+"F11.wireOp",EDGE,"E12.3");Q0=makeQuery(id+"F12.boolean.opBoolean","COPY",EDGE,{"disambiguationData":[TD([makeQuery(id+"F9.opExtrude","CAP_FACE",FACE,{"disambiguationData":[OSD([subQ11,subQ10,subQ9,subQ8,subQ7,subQ6,subQ5,subQ4,subQ3,subQ2,subQ1,subQ0])],"isStart":true})])],"derivedFrom":makeQuery(id+"F12.opExtrude","SWEPT_EDGE",EDGE,{"disambiguationData":[OSD([subQ13,subQ12])]})});}
            var Q1;
            {var subQ0=sQuery(id+"F8.wireOp",EDGE,"E5");var subQ1=sQuery(id+"F8.wireOp",EDGE,"mOqyP8SL-vEXn-Shjf-BXRA-A4QvbKXMYqA2");var subQ2=sQuery(id+"F8.wireOp",EDGE,"4i0MoKHX-XmxI-cSmD-P7XZ-JZizBw6dTzRK");var subQ3=sQuery(id+"F8.wireOp",EDGE,"orgWuDI4-4pWB-4aS4-cs57-z0Hx2wF69UBw");var subQ4=sQuery(id+"F8.wireOp",EDGE,"E4");var subQ5=sQuery(id+"F8.wireOp",EDGE,"E3");var subQ6=sQuery(id+"F8.wireOp",EDGE,"E2");var subQ7=sQuery(id+"F8.wireOp",EDGE,"Jx2hsfEg-rsGK-g6mN-gGwm-UTiYR1x8r5xO");var subQ8=sQuery(id+"F8.wireOp",EDGE,"7PxteJ0w-hNWy-X14L-V5LG-c6Ao6gPeCcrO");var subQ9=sQuery(id+"F8.wireOp",EDGE,"4ElTsRrF-d6Ta-Xpu3-N1rJ-FU14qHi0ozwZ");var subQ10=sQuery(id+"F8.wireOp",EDGE,"E1");var subQ11=sQuery(id+"F8.wireOp",EDGE,"E0");var subQ12=sQuery(id+"F11.wireOp",EDGE,"E12.3");var subQ13=sQuery(id+"F11.wireOp",EDGE,"E13");Q1=makeQuery(id+"F12.boolean.opBoolean","COPY",EDGE,{"disambiguationData":[TD([makeQuery(id+"F10.opExtrude","CAP_FACE",FACE,{"disambiguationData":[OSD([subQ11,subQ10,subQ9,subQ8,subQ7,subQ6,subQ5,subQ4,subQ3,subQ2,subQ1,subQ0])],"isStart":true})])],"derivedFrom":makeQuery(id+"F12.opExtrude","SWEPT_EDGE",EDGE,{"disambiguationData":[OSD([subQ12,subQ13])]})});}
            var Q2;
            {var subQ0=sQuery(id+"F8.wireOp",EDGE,"E5");var subQ1=sQuery(id+"F8.wireOp",EDGE,"mOqyP8SL-vEXn-Shjf-BXRA-A4QvbKXMYqA2");var subQ2=sQuery(id+"F8.wireOp",EDGE,"4i0MoKHX-XmxI-cSmD-P7XZ-JZizBw6dTzRK");var subQ3=sQuery(id+"F8.wireOp",EDGE,"orgWuDI4-4pWB-4aS4-cs57-z0Hx2wF69UBw");var subQ4=sQuery(id+"F8.wireOp",EDGE,"E4");var subQ5=sQuery(id+"F8.wireOp",EDGE,"E3");var subQ6=sQuery(id+"F8.wireOp",EDGE,"E2");var subQ7=sQuery(id+"F8.wireOp",EDGE,"Jx2hsfEg-rsGK-g6mN-gGwm-UTiYR1x8r5xO");var subQ8=sQuery(id+"F8.wireOp",EDGE,"7PxteJ0w-hNWy-X14L-V5LG-c6Ao6gPeCcrO");var subQ9=sQuery(id+"F8.wireOp",EDGE,"4ElTsRrF-d6Ta-Xpu3-N1rJ-FU14qHi0ozwZ");var subQ10=sQuery(id+"F8.wireOp",EDGE,"E1");var subQ11=sQuery(id+"F8.wireOp",EDGE,"E0");Q2=makeQuery(id+"F16.boolean.opBoolean","INTERSECT",EDGE,{"derivedFrom":[makeQuery(id+"F12.boolean.opBoolean","COPY",FACE,{"disambiguationData":[TD([makeQuery(id+"F10.opExtrude","CAP_FACE",FACE,{"disambiguationData":[OSD([subQ11,subQ10,subQ9,subQ8,subQ7,subQ6,subQ5,subQ4,subQ3,subQ2,subQ1,subQ0])],"isStart":true})])],"derivedFrom":makeQuery(id+"F12.opExtrude","SWEPT_FACE",FACE,{"disambiguationData":[OSD([sQuery(id+"F11.wireOp",EDGE,"E12.3")])]})}),makeQuery(id+"F16.opExtrude","SWEPT_FACE",FACE,{"disambiguationData":[OSD([sQuery(id+"F15.wireOp",EDGE,"E24.bottom")])]})]});}
            var Q3;
            {var subQ0=sQuery(id+"F8.wireOp",EDGE,"E5");var subQ1=sQuery(id+"F8.wireOp",EDGE,"mOqyP8SL-vEXn-Shjf-BXRA-A4QvbKXMYqA2");var subQ2=sQuery(id+"F8.wireOp",EDGE,"4i0MoKHX-XmxI-cSmD-P7XZ-JZizBw6dTzRK");var subQ3=sQuery(id+"F8.wireOp",EDGE,"orgWuDI4-4pWB-4aS4-cs57-z0Hx2wF69UBw");var subQ4=sQuery(id+"F8.wireOp",EDGE,"E4");var subQ5=sQuery(id+"F8.wireOp",EDGE,"E3");var subQ6=sQuery(id+"F8.wireOp",EDGE,"E2");var subQ7=sQuery(id+"F8.wireOp",EDGE,"Jx2hsfEg-rsGK-g6mN-gGwm-UTiYR1x8r5xO");var subQ8=sQuery(id+"F8.wireOp",EDGE,"7PxteJ0w-hNWy-X14L-V5LG-c6Ao6gPeCcrO");var subQ9=sQuery(id+"F8.wireOp",EDGE,"4ElTsRrF-d6Ta-Xpu3-N1rJ-FU14qHi0ozwZ");var subQ10=sQuery(id+"F8.wireOp",EDGE,"E1");var subQ11=sQuery(id+"F8.wireOp",EDGE,"E0");Q3=makeQuery(id+"F16.boolean.opBoolean","INTERSECT",EDGE,{"derivedFrom":[makeQuery(id+"F12.boolean.opBoolean","COPY",FACE,{"disambiguationData":[TD([makeQuery(id+"F9.opExtrude","CAP_FACE",FACE,{"disambiguationData":[OSD([subQ11,subQ10,subQ9,subQ8,subQ7,subQ6,subQ5,subQ4,subQ3,subQ2,subQ1,subQ0])],"isStart":true})])],"derivedFrom":makeQuery(id+"F12.opExtrude","SWEPT_FACE",FACE,{"disambiguationData":[OSD([sQuery(id+"F11.wireOp",EDGE,"E12.3")])]})}),makeQuery(id+"F16.opExtrude","SWEPT_FACE",FACE,{"disambiguationData":[OSD([sQuery(id+"F15.wireOp",EDGE,"E24.bottom")])]})]});}
            var Q4;
            {var subQ0=sQuery(id+"F8.wireOp",EDGE,"E5");var subQ1=sQuery(id+"F8.wireOp",EDGE,"mOqyP8SL-vEXn-Shjf-BXRA-A4QvbKXMYqA2");var subQ2=sQuery(id+"F8.wireOp",EDGE,"4i0MoKHX-XmxI-cSmD-P7XZ-JZizBw6dTzRK");var subQ3=sQuery(id+"F8.wireOp",EDGE,"orgWuDI4-4pWB-4aS4-cs57-z0Hx2wF69UBw");var subQ4=sQuery(id+"F8.wireOp",EDGE,"E4");var subQ5=sQuery(id+"F8.wireOp",EDGE,"E3");var subQ6=sQuery(id+"F8.wireOp",EDGE,"E2");var subQ7=sQuery(id+"F8.wireOp",EDGE,"Jx2hsfEg-rsGK-g6mN-gGwm-UTiYR1x8r5xO");var subQ8=sQuery(id+"F8.wireOp",EDGE,"7PxteJ0w-hNWy-X14L-V5LG-c6Ao6gPeCcrO");var subQ9=sQuery(id+"F8.wireOp",EDGE,"4ElTsRrF-d6Ta-Xpu3-N1rJ-FU14qHi0ozwZ");var subQ10=sQuery(id+"F8.wireOp",EDGE,"E1");var subQ11=sQuery(id+"F8.wireOp",EDGE,"E0");var subQ12=sQuery(id+"F11.wireOp",EDGE,"E12.2");var subQ13=sQuery(id+"F11.wireOp",EDGE,"E12.3");Q4=makeQuery(id+"F12.boolean.opBoolean","COPY",EDGE,{"disambiguationData":[TD([makeQuery(id+"F9.opExtrude","CAP_FACE",FACE,{"disambiguationData":[OSD([subQ11,subQ10,subQ9,subQ8,subQ7,subQ6,subQ5,subQ4,subQ3,subQ2,subQ1,subQ0])],"isStart":true})])],"derivedFrom":makeQuery(id+"F12.opExtrude","SWEPT_EDGE",EDGE,{"disambiguationData":[OSD([subQ12,subQ13])]})});}
            var Q5;
            {var subQ0=sQuery(id+"F8.wireOp",EDGE,"E5");var subQ1=sQuery(id+"F8.wireOp",EDGE,"mOqyP8SL-vEXn-Shjf-BXRA-A4QvbKXMYqA2");var subQ2=sQuery(id+"F8.wireOp",EDGE,"4i0MoKHX-XmxI-cSmD-P7XZ-JZizBw6dTzRK");var subQ3=sQuery(id+"F8.wireOp",EDGE,"orgWuDI4-4pWB-4aS4-cs57-z0Hx2wF69UBw");var subQ4=sQuery(id+"F8.wireOp",EDGE,"E4");var subQ5=sQuery(id+"F8.wireOp",EDGE,"E3");var subQ6=sQuery(id+"F8.wireOp",EDGE,"E2");var subQ7=sQuery(id+"F8.wireOp",EDGE,"Jx2hsfEg-rsGK-g6mN-gGwm-UTiYR1x8r5xO");var subQ8=sQuery(id+"F8.wireOp",EDGE,"7PxteJ0w-hNWy-X14L-V5LG-c6Ao6gPeCcrO");var subQ9=sQuery(id+"F8.wireOp",EDGE,"4ElTsRrF-d6Ta-Xpu3-N1rJ-FU14qHi0ozwZ");var subQ10=sQuery(id+"F8.wireOp",EDGE,"E1");var subQ11=sQuery(id+"F8.wireOp",EDGE,"E0");var subQ12=sQuery(id+"F11.wireOp",EDGE,"E12.2");var subQ13=sQuery(id+"F11.wireOp",EDGE,"E12.3");Q5=makeQuery(id+"F12.boolean.opBoolean","COPY",EDGE,{"disambiguationData":[TD([makeQuery(id+"F10.opExtrude","CAP_FACE",FACE,{"disambiguationData":[OSD([subQ11,subQ10,subQ9,subQ8,subQ7,subQ6,subQ5,subQ4,subQ3,subQ2,subQ1,subQ0])],"isStart":true})])],"derivedFrom":makeQuery(id+"F12.opExtrude","SWEPT_EDGE",EDGE,{"disambiguationData":[OSD([subQ12,subQ13])]})});}
            var Q6;
            {var subQ0=sQuery(id+"F8.wireOp",EDGE,"E0");var subQ1=sQuery(id+"F11.wireOp",EDGE,"E13");Q6=makeQuery(id+"F12.boolean.opBoolean","COPY",EDGE,{"disambiguationData":[topologyDisambiguationEdgeConnected([makeQuery(id+"F9.opExtrude","SWEPT_FACE",FACE,{"disambiguationData":[OSD([subQ0])]})])],"derivedFrom":makeQuery(id+"F12.opExtrude","SWEPT_EDGE",EDGE,{"disambiguationData":[OSD([subQ0,subQ1,sQuery(id+"F11.wireOp",EDGE,"E14")])]})});}
            var Q7;
            {var subQ0=sQuery(id+"F8.wireOp",EDGE,"E0");var subQ1=sQuery(id+"F11.wireOp",EDGE,"E13");Q7=makeQuery(id+"F12.boolean.opBoolean","COPY",EDGE,{"disambiguationData":[topologyDisambiguationEdgeConnected([makeQuery(id+"F10.opExtrude","SWEPT_FACE",FACE,{"disambiguationData":[OSD([subQ0])]})])],"derivedFrom":makeQuery(id+"F12.opExtrude","SWEPT_EDGE",EDGE,{"disambiguationData":[OSD([subQ0,subQ1,sQuery(id+"F11.wireOp",EDGE,"E14")])]})});}
            var Q8;
            {var subQ0=sQuery(id+"F8.wireOp",EDGE,"E5");var subQ1=sQuery(id+"F8.wireOp",EDGE,"mOqyP8SL-vEXn-Shjf-BXRA-A4QvbKXMYqA2");var subQ2=sQuery(id+"F8.wireOp",EDGE,"4i0MoKHX-XmxI-cSmD-P7XZ-JZizBw6dTzRK");var subQ3=sQuery(id+"F8.wireOp",EDGE,"orgWuDI4-4pWB-4aS4-cs57-z0Hx2wF69UBw");var subQ4=sQuery(id+"F8.wireOp",EDGE,"E4");var subQ5=sQuery(id+"F8.wireOp",EDGE,"E3");var subQ6=sQuery(id+"F8.wireOp",EDGE,"E2");var subQ7=sQuery(id+"F8.wireOp",EDGE,"Jx2hsfEg-rsGK-g6mN-gGwm-UTiYR1x8r5xO");var subQ8=sQuery(id+"F8.wireOp",EDGE,"7PxteJ0w-hNWy-X14L-V5LG-c6Ao6gPeCcrO");var subQ9=sQuery(id+"F8.wireOp",EDGE,"4ElTsRrF-d6Ta-Xpu3-N1rJ-FU14qHi0ozwZ");var subQ10=sQuery(id+"F8.wireOp",EDGE,"E1");var subQ11=sQuery(id+"F8.wireOp",EDGE,"E0");var subQ12=sQuery(id+"F11.wireOp",EDGE,"E12.1");var subQ13=sQuery(id+"F11.wireOp",EDGE,"E12.2");Q8=makeQuery(id+"F12.boolean.opBoolean","COPY",EDGE,{"disambiguationData":[TD([makeQuery(id+"F10.opExtrude","CAP_FACE",FACE,{"disambiguationData":[OSD([subQ11,subQ10,subQ9,subQ8,subQ7,subQ6,subQ5,subQ4,subQ3,subQ2,subQ1,subQ0])],"isStart":true})])],"derivedFrom":makeQuery(id+"F12.opExtrude","SWEPT_EDGE",EDGE,{"disambiguationData":[OSD([subQ12,subQ13])]})});}
            var Q9;
            {var subQ0=sQuery(id+"F8.wireOp",EDGE,"E5");var subQ1=sQuery(id+"F8.wireOp",EDGE,"mOqyP8SL-vEXn-Shjf-BXRA-A4QvbKXMYqA2");var subQ2=sQuery(id+"F8.wireOp",EDGE,"4i0MoKHX-XmxI-cSmD-P7XZ-JZizBw6dTzRK");var subQ3=sQuery(id+"F8.wireOp",EDGE,"orgWuDI4-4pWB-4aS4-cs57-z0Hx2wF69UBw");var subQ4=sQuery(id+"F8.wireOp",EDGE,"E4");var subQ5=sQuery(id+"F8.wireOp",EDGE,"E3");var subQ6=sQuery(id+"F8.wireOp",EDGE,"E2");var subQ7=sQuery(id+"F8.wireOp",EDGE,"Jx2hsfEg-rsGK-g6mN-gGwm-UTiYR1x8r5xO");var subQ8=sQuery(id+"F8.wireOp",EDGE,"7PxteJ0w-hNWy-X14L-V5LG-c6Ao6gPeCcrO");var subQ9=sQuery(id+"F8.wireOp",EDGE,"4ElTsRrF-d6Ta-Xpu3-N1rJ-FU14qHi0ozwZ");var subQ10=sQuery(id+"F8.wireOp",EDGE,"E1");var subQ11=sQuery(id+"F8.wireOp",EDGE,"E0");Q9=makeQuery(id+"F16.boolean.opBoolean","INTERSECT",EDGE,{"derivedFrom":[makeQuery(id+"F12.boolean.opBoolean","COPY",FACE,{"disambiguationData":[TD([makeQuery(id+"F10.opExtrude","CAP_FACE",FACE,{"disambiguationData":[OSD([subQ11,subQ10,subQ9,subQ8,subQ7,subQ6,subQ5,subQ4,subQ3,subQ2,subQ1,subQ0])],"isStart":true})])],"derivedFrom":makeQuery(id+"F12.opExtrude","SWEPT_FACE",FACE,{"disambiguationData":[OSD([sQuery(id+"F11.wireOp",EDGE,"E12.1")])]})}),makeQuery(id+"F16.opExtrude","SWEPT_FACE",FACE,{"disambiguationData":[OSD([sQuery(id+"F15.wireOp",EDGE,"E24.top")])]})]});}
            var Q10;
            {var subQ0=sQuery(id+"F8.wireOp",EDGE,"E5");var subQ1=sQuery(id+"F8.wireOp",EDGE,"mOqyP8SL-vEXn-Shjf-BXRA-A4QvbKXMYqA2");var subQ2=sQuery(id+"F8.wireOp",EDGE,"4i0MoKHX-XmxI-cSmD-P7XZ-JZizBw6dTzRK");var subQ3=sQuery(id+"F8.wireOp",EDGE,"orgWuDI4-4pWB-4aS4-cs57-z0Hx2wF69UBw");var subQ4=sQuery(id+"F8.wireOp",EDGE,"E4");var subQ5=sQuery(id+"F8.wireOp",EDGE,"E3");var subQ6=sQuery(id+"F8.wireOp",EDGE,"E2");var subQ7=sQuery(id+"F8.wireOp",EDGE,"Jx2hsfEg-rsGK-g6mN-gGwm-UTiYR1x8r5xO");var subQ8=sQuery(id+"F8.wireOp",EDGE,"7PxteJ0w-hNWy-X14L-V5LG-c6Ao6gPeCcrO");var subQ9=sQuery(id+"F8.wireOp",EDGE,"4ElTsRrF-d6Ta-Xpu3-N1rJ-FU14qHi0ozwZ");var subQ10=sQuery(id+"F8.wireOp",EDGE,"E1");var subQ11=sQuery(id+"F8.wireOp",EDGE,"E0");Q10=makeQuery(id+"F16.boolean.opBoolean","INTERSECT",EDGE,{"derivedFrom":[makeQuery(id+"F12.boolean.opBoolean","COPY",FACE,{"disambiguationData":[TD([makeQuery(id+"F9.opExtrude","CAP_FACE",FACE,{"disambiguationData":[OSD([subQ11,subQ10,subQ9,subQ8,subQ7,subQ6,subQ5,subQ4,subQ3,subQ2,subQ1,subQ0])],"isStart":true})])],"derivedFrom":makeQuery(id+"F12.opExtrude","SWEPT_FACE",FACE,{"disambiguationData":[OSD([sQuery(id+"F11.wireOp",EDGE,"E12.1")])]})}),makeQuery(id+"F16.opExtrude","SWEPT_FACE",FACE,{"disambiguationData":[OSD([sQuery(id+"F15.wireOp",EDGE,"E24.top")])]})]});}
            var Q11;
            {var subQ0=sQuery(id+"F8.wireOp",EDGE,"E5");var subQ1=sQuery(id+"F8.wireOp",EDGE,"mOqyP8SL-vEXn-Shjf-BXRA-A4QvbKXMYqA2");var subQ2=sQuery(id+"F8.wireOp",EDGE,"4i0MoKHX-XmxI-cSmD-P7XZ-JZizBw6dTzRK");var subQ3=sQuery(id+"F8.wireOp",EDGE,"orgWuDI4-4pWB-4aS4-cs57-z0Hx2wF69UBw");var subQ4=sQuery(id+"F8.wireOp",EDGE,"E4");var subQ5=sQuery(id+"F8.wireOp",EDGE,"E3");var subQ6=sQuery(id+"F8.wireOp",EDGE,"E2");var subQ7=sQuery(id+"F8.wireOp",EDGE,"Jx2hsfEg-rsGK-g6mN-gGwm-UTiYR1x8r5xO");var subQ8=sQuery(id+"F8.wireOp",EDGE,"7PxteJ0w-hNWy-X14L-V5LG-c6Ao6gPeCcrO");var subQ9=sQuery(id+"F8.wireOp",EDGE,"4ElTsRrF-d6Ta-Xpu3-N1rJ-FU14qHi0ozwZ");var subQ10=sQuery(id+"F8.wireOp",EDGE,"E1");var subQ11=sQuery(id+"F8.wireOp",EDGE,"E0");var subQ12=sQuery(id+"F11.wireOp",EDGE,"E12.1");var subQ13=sQuery(id+"F11.wireOp",EDGE,"E12.2");Q11=makeQuery(id+"F12.boolean.opBoolean","COPY",EDGE,{"disambiguationData":[TD([makeQuery(id+"F9.opExtrude","CAP_FACE",FACE,{"disambiguationData":[OSD([subQ11,subQ10,subQ9,subQ8,subQ7,subQ6,subQ5,subQ4,subQ3,subQ2,subQ1,subQ0])],"isStart":true})])],"derivedFrom":makeQuery(id+"F12.opExtrude","SWEPT_EDGE",EDGE,{"disambiguationData":[OSD([subQ12,subQ13])]})});}
            var Q12;
            {var subQ0=sQuery(id+"F8.wireOp",EDGE,"E5");var subQ1=sQuery(id+"F8.wireOp",EDGE,"mOqyP8SL-vEXn-Shjf-BXRA-A4QvbKXMYqA2");var subQ2=sQuery(id+"F8.wireOp",EDGE,"4i0MoKHX-XmxI-cSmD-P7XZ-JZizBw6dTzRK");var subQ3=sQuery(id+"F8.wireOp",EDGE,"orgWuDI4-4pWB-4aS4-cs57-z0Hx2wF69UBw");var subQ4=sQuery(id+"F8.wireOp",EDGE,"E4");var subQ5=sQuery(id+"F8.wireOp",EDGE,"E3");var subQ6=sQuery(id+"F8.wireOp",EDGE,"E2");var subQ7=sQuery(id+"F8.wireOp",EDGE,"Jx2hsfEg-rsGK-g6mN-gGwm-UTiYR1x8r5xO");var subQ8=sQuery(id+"F8.wireOp",EDGE,"7PxteJ0w-hNWy-X14L-V5LG-c6Ao6gPeCcrO");var subQ9=sQuery(id+"F8.wireOp",EDGE,"4ElTsRrF-d6Ta-Xpu3-N1rJ-FU14qHi0ozwZ");var subQ10=sQuery(id+"F8.wireOp",EDGE,"E1");var subQ11=sQuery(id+"F8.wireOp",EDGE,"E0");var subQ12=sQuery(id+"F11.wireOp",EDGE,"E12.1");var subQ13=sQuery(id+"F11.wireOp",EDGE,"E12.0");Q12=makeQuery(id+"F12.boolean.opBoolean","COPY",EDGE,{"disambiguationData":[TD([makeQuery(id+"F10.opExtrude","CAP_FACE",FACE,{"disambiguationData":[OSD([subQ11,subQ10,subQ9,subQ8,subQ7,subQ6,subQ5,subQ4,subQ3,subQ2,subQ1,subQ0])],"isStart":true})])],"derivedFrom":makeQuery(id+"F12.opExtrude","SWEPT_EDGE",EDGE,{"disambiguationData":[OSD([subQ13,subQ12])]})});}
            var Q13;
            {var subQ0=sQuery(id+"F8.wireOp",EDGE,"E5");var subQ1=sQuery(id+"F8.wireOp",EDGE,"mOqyP8SL-vEXn-Shjf-BXRA-A4QvbKXMYqA2");var subQ2=sQuery(id+"F8.wireOp",EDGE,"4i0MoKHX-XmxI-cSmD-P7XZ-JZizBw6dTzRK");var subQ3=sQuery(id+"F8.wireOp",EDGE,"orgWuDI4-4pWB-4aS4-cs57-z0Hx2wF69UBw");var subQ4=sQuery(id+"F8.wireOp",EDGE,"E4");var subQ5=sQuery(id+"F8.wireOp",EDGE,"E3");var subQ6=sQuery(id+"F8.wireOp",EDGE,"E2");var subQ7=sQuery(id+"F8.wireOp",EDGE,"Jx2hsfEg-rsGK-g6mN-gGwm-UTiYR1x8r5xO");var subQ8=sQuery(id+"F8.wireOp",EDGE,"7PxteJ0w-hNWy-X14L-V5LG-c6Ao6gPeCcrO");var subQ9=sQuery(id+"F8.wireOp",EDGE,"4ElTsRrF-d6Ta-Xpu3-N1rJ-FU14qHi0ozwZ");var subQ10=sQuery(id+"F8.wireOp",EDGE,"E1");var subQ11=sQuery(id+"F8.wireOp",EDGE,"E0");var subQ12=sQuery(id+"F11.wireOp",EDGE,"E12.1");var subQ13=sQuery(id+"F11.wireOp",EDGE,"E12.0");Q13=makeQuery(id+"F12.boolean.opBoolean","COPY",EDGE,{"disambiguationData":[TD([makeQuery(id+"F9.opExtrude","CAP_FACE",FACE,{"disambiguationData":[OSD([subQ11,subQ10,subQ9,subQ8,subQ7,subQ6,subQ5,subQ4,subQ3,subQ2,subQ1,subQ0])],"isStart":true})])],"derivedFrom":makeQuery(id+"F12.opExtrude","SWEPT_EDGE",EDGE,{"disambiguationData":[OSD([subQ13,subQ12])]})});}
            var Q14;
            {var subQ0=sQuery(id+"F8.wireOp",EDGE,"E5");var subQ1=sQuery(id+"F8.wireOp",EDGE,"mOqyP8SL-vEXn-Shjf-BXRA-A4QvbKXMYqA2");var subQ2=sQuery(id+"F8.wireOp",EDGE,"4i0MoKHX-XmxI-cSmD-P7XZ-JZizBw6dTzRK");var subQ3=sQuery(id+"F8.wireOp",EDGE,"orgWuDI4-4pWB-4aS4-cs57-z0Hx2wF69UBw");var subQ4=sQuery(id+"F8.wireOp",EDGE,"E4");var subQ5=sQuery(id+"F8.wireOp",EDGE,"E3");var subQ6=sQuery(id+"F8.wireOp",EDGE,"E2");var subQ7=sQuery(id+"F8.wireOp",EDGE,"Jx2hsfEg-rsGK-g6mN-gGwm-UTiYR1x8r5xO");var subQ8=sQuery(id+"F8.wireOp",EDGE,"7PxteJ0w-hNWy-X14L-V5LG-c6Ao6gPeCcrO");var subQ9=sQuery(id+"F8.wireOp",EDGE,"4ElTsRrF-d6Ta-Xpu3-N1rJ-FU14qHi0ozwZ");var subQ10=sQuery(id+"F8.wireOp",EDGE,"E1");var subQ11=sQuery(id+"F8.wireOp",EDGE,"E0");var subQ12=sQuery(id+"F11.wireOp",EDGE,"E12.0");var subQ13=sQuery(id+"F11.wireOp",EDGE,"E12.7");Q14=makeQuery(id+"F12.boolean.opBoolean","COPY",EDGE,{"disambiguationData":[TD([makeQuery(id+"F9.opExtrude","CAP_FACE",FACE,{"disambiguationData":[OSD([subQ11,subQ10,subQ9,subQ8,subQ7,subQ6,subQ5,subQ4,subQ3,subQ2,subQ1,subQ0])],"isStart":true})])],"derivedFrom":makeQuery(id+"F12.opExtrude","SWEPT_EDGE",EDGE,{"disambiguationData":[OSD([subQ12,subQ13])]})});}
            var Q15;
            {var subQ0=sQuery(id+"F8.wireOp",EDGE,"E5");var subQ1=sQuery(id+"F8.wireOp",EDGE,"mOqyP8SL-vEXn-Shjf-BXRA-A4QvbKXMYqA2");var subQ2=sQuery(id+"F8.wireOp",EDGE,"4i0MoKHX-XmxI-cSmD-P7XZ-JZizBw6dTzRK");var subQ3=sQuery(id+"F8.wireOp",EDGE,"orgWuDI4-4pWB-4aS4-cs57-z0Hx2wF69UBw");var subQ4=sQuery(id+"F8.wireOp",EDGE,"E4");var subQ5=sQuery(id+"F8.wireOp",EDGE,"E3");var subQ6=sQuery(id+"F8.wireOp",EDGE,"E2");var subQ7=sQuery(id+"F8.wireOp",EDGE,"Jx2hsfEg-rsGK-g6mN-gGwm-UTiYR1x8r5xO");var subQ8=sQuery(id+"F8.wireOp",EDGE,"7PxteJ0w-hNWy-X14L-V5LG-c6Ao6gPeCcrO");var subQ9=sQuery(id+"F8.wireOp",EDGE,"4ElTsRrF-d6Ta-Xpu3-N1rJ-FU14qHi0ozwZ");var subQ10=sQuery(id+"F8.wireOp",EDGE,"E1");var subQ11=sQuery(id+"F8.wireOp",EDGE,"E0");var subQ12=sQuery(id+"F11.wireOp",EDGE,"E12.0");var subQ13=sQuery(id+"F11.wireOp",EDGE,"E12.7");Q15=makeQuery(id+"F12.boolean.opBoolean","COPY",EDGE,{"disambiguationData":[TD([makeQuery(id+"F10.opExtrude","CAP_FACE",FACE,{"disambiguationData":[OSD([subQ11,subQ10,subQ9,subQ8,subQ7,subQ6,subQ5,subQ4,subQ3,subQ2,subQ1,subQ0])],"isStart":true})])],"derivedFrom":makeQuery(id+"F12.opExtrude","SWEPT_EDGE",EDGE,{"disambiguationData":[OSD([subQ12,subQ13])]})});}
            var Q16;
            {var subQ0=sQuery(id+"F8.wireOp",EDGE,"E5");var subQ1=sQuery(id+"F8.wireOp",EDGE,"mOqyP8SL-vEXn-Shjf-BXRA-A4QvbKXMYqA2");var subQ2=sQuery(id+"F8.wireOp",EDGE,"4i0MoKHX-XmxI-cSmD-P7XZ-JZizBw6dTzRK");var subQ3=sQuery(id+"F8.wireOp",EDGE,"orgWuDI4-4pWB-4aS4-cs57-z0Hx2wF69UBw");var subQ4=sQuery(id+"F8.wireOp",EDGE,"E4");var subQ5=sQuery(id+"F8.wireOp",EDGE,"E3");var subQ6=sQuery(id+"F8.wireOp",EDGE,"E2");var subQ7=sQuery(id+"F8.wireOp",EDGE,"Jx2hsfEg-rsGK-g6mN-gGwm-UTiYR1x8r5xO");var subQ8=sQuery(id+"F8.wireOp",EDGE,"7PxteJ0w-hNWy-X14L-V5LG-c6Ao6gPeCcrO");var subQ9=sQuery(id+"F8.wireOp",EDGE,"4ElTsRrF-d6Ta-Xpu3-N1rJ-FU14qHi0ozwZ");var subQ10=sQuery(id+"F8.wireOp",EDGE,"E1");var subQ11=sQuery(id+"F8.wireOp",EDGE,"E0");var subQ12=sQuery(id+"F11.wireOp",EDGE,"E15");var subQ13=sQuery(id+"F11.wireOp",EDGE,"E12.7");Q16=makeQuery(id+"F12.boolean.opBoolean","COPY",EDGE,{"disambiguationData":[TD([makeQuery(id+"F10.opExtrude","CAP_FACE",FACE,{"disambiguationData":[OSD([subQ11,subQ10,subQ9,subQ8,subQ7,subQ6,subQ5,subQ4,subQ3,subQ2,subQ1,subQ0])],"isStart":true})])],"derivedFrom":makeQuery(id+"F12.opExtrude","SWEPT_EDGE",EDGE,{"disambiguationData":[OSD([subQ13,subQ12])]})});}
            var Q17;
            {var subQ0=sQuery(id+"F8.wireOp",EDGE,"E5");var subQ1=sQuery(id+"F8.wireOp",EDGE,"mOqyP8SL-vEXn-Shjf-BXRA-A4QvbKXMYqA2");var subQ2=sQuery(id+"F8.wireOp",EDGE,"4i0MoKHX-XmxI-cSmD-P7XZ-JZizBw6dTzRK");var subQ3=sQuery(id+"F8.wireOp",EDGE,"orgWuDI4-4pWB-4aS4-cs57-z0Hx2wF69UBw");var subQ4=sQuery(id+"F8.wireOp",EDGE,"E4");var subQ5=sQuery(id+"F8.wireOp",EDGE,"E3");var subQ6=sQuery(id+"F8.wireOp",EDGE,"E2");var subQ7=sQuery(id+"F8.wireOp",EDGE,"Jx2hsfEg-rsGK-g6mN-gGwm-UTiYR1x8r5xO");var subQ8=sQuery(id+"F8.wireOp",EDGE,"7PxteJ0w-hNWy-X14L-V5LG-c6Ao6gPeCcrO");var subQ9=sQuery(id+"F8.wireOp",EDGE,"4ElTsRrF-d6Ta-Xpu3-N1rJ-FU14qHi0ozwZ");var subQ10=sQuery(id+"F8.wireOp",EDGE,"E1");var subQ11=sQuery(id+"F8.wireOp",EDGE,"E0");var subQ12=sQuery(id+"F11.wireOp",EDGE,"E12.7");var subQ13=sQuery(id+"F11.wireOp",EDGE,"E15");Q17=makeQuery(id+"F12.boolean.opBoolean","COPY",EDGE,{"disambiguationData":[TD([makeQuery(id+"F9.opExtrude","CAP_FACE",FACE,{"disambiguationData":[OSD([subQ11,subQ10,subQ9,subQ8,subQ7,subQ6,subQ5,subQ4,subQ3,subQ2,subQ1,subQ0])],"isStart":true})])],"derivedFrom":makeQuery(id+"F12.opExtrude","SWEPT_EDGE",EDGE,{"disambiguationData":[OSD([subQ12,subQ13])]})});}
            var Q18;
            {var subQ0=sQuery(id+"F8.wireOp",EDGE,"E2");var subQ1=sQuery(id+"F11.wireOp",EDGE,"E15");Q18=makeQuery(id+"F12.boolean.opBoolean","COPY",EDGE,{"disambiguationData":[topologyDisambiguationEdgeConnected([makeQuery(id+"F9.opExtrude","SWEPT_FACE",FACE,{"disambiguationData":[OSD([subQ0])]})])],"derivedFrom":makeQuery(id+"F12.opExtrude","SWEPT_EDGE",EDGE,{"disambiguationData":[OSD([subQ0,subQ1,sQuery(id+"F11.wireOp",EDGE,"E16")])]})});}
            var Q19;
            {var subQ0=sQuery(id+"F8.wireOp",EDGE,"E2");var subQ1=sQuery(id+"F11.wireOp",EDGE,"E15");Q19=makeQuery(id+"F12.boolean.opBoolean","COPY",EDGE,{"disambiguationData":[topologyDisambiguationEdgeConnected([makeQuery(id+"F10.opExtrude","SWEPT_FACE",FACE,{"disambiguationData":[OSD([subQ0])]})])],"derivedFrom":makeQuery(id+"F12.opExtrude","SWEPT_EDGE",EDGE,{"disambiguationData":[OSD([subQ0,subQ1,sQuery(id+"F11.wireOp",EDGE,"E16")])]})});}
            var Q20;
            Q20=makeQuery(id+"F10.opExtrude","SWEPT_EDGE",EDGE,{"disambiguationData":[OSD([sQuery(id+"F8.wireOp",EDGE,"E2"),sQuery(id+"F8.wireOp",EDGE,"E3")])]});
            var Q21;
            Q21=makeQuery(id+"F9.opExtrude","SWEPT_EDGE",EDGE,{"disambiguationData":[OSD([sQuery(id+"F8.wireOp",EDGE,"E2"),sQuery(id+"F8.wireOp",EDGE,"E3")])]});
            var Q22;
            Q22=makeQuery(id+"F9.opExtrude","SWEPT_EDGE",EDGE,{"disambiguationData":[OSD([sQuery(id+"F8.wireOp",EDGE,"E3"),sQuery(id+"F8.wireOp",EDGE,"E4")])]});
            var Q23;
            Q23=makeQuery(id+"F9.opExtrude","SWEPT_EDGE",EDGE,{"disambiguationData":[OSD([sQuery(id+"F8.wireOp",EDGE,"E4"),sQuery(id+"F8.wireOp",EDGE,"orgWuDI4-4pWB-4aS4-cs57-z0Hx2wF69UBw")])]});
            var Q24;
            Q24=makeQuery(id+"F9.opExtrude","SWEPT_EDGE",EDGE,{"disambiguationData":[OSD([sQuery(id+"F8.wireOp",EDGE,"orgWuDI4-4pWB-4aS4-cs57-z0Hx2wF69UBw"),sQuery(id+"F8.wireOp",EDGE,"4i0MoKHX-XmxI-cSmD-P7XZ-JZizBw6dTzRK")])]});
            var Q25;
            Q25=makeQuery(id+"F10.opExtrude","SWEPT_EDGE",EDGE,{"disambiguationData":[OSD([sQuery(id+"F8.wireOp",EDGE,"orgWuDI4-4pWB-4aS4-cs57-z0Hx2wF69UBw"),sQuery(id+"F8.wireOp",EDGE,"4i0MoKHX-XmxI-cSmD-P7XZ-JZizBw6dTzRK")])]});
            var Q26;
            Q26=makeQuery(id+"F9.opExtrude","SWEPT_EDGE",EDGE,{"disambiguationData":[OSD([sQuery(id+"F8.wireOp",EDGE,"4i0MoKHX-XmxI-cSmD-P7XZ-JZizBw6dTzRK"),sQuery(id+"F8.wireOp",EDGE,"mOqyP8SL-vEXn-Shjf-BXRA-A4QvbKXMYqA2")])]});
            var Q27;
            Q27=makeQuery(id+"F10.opExtrude","SWEPT_EDGE",EDGE,{"disambiguationData":[OSD([sQuery(id+"F8.wireOp",EDGE,"4i0MoKHX-XmxI-cSmD-P7XZ-JZizBw6dTzRK"),sQuery(id+"F8.wireOp",EDGE,"mOqyP8SL-vEXn-Shjf-BXRA-A4QvbKXMYqA2")])]});
            var Q28;
            Q28=makeQuery(id+"F9.opExtrude","SWEPT_EDGE",EDGE,{"disambiguationData":[OSD([sQuery(id+"F8.wireOp",EDGE,"mOqyP8SL-vEXn-Shjf-BXRA-A4QvbKXMYqA2"),sQuery(id+"F8.wireOp",EDGE,"E5")])]});
            var Q29;
            Q29=makeQuery(id+"F10.opExtrude","SWEPT_EDGE",EDGE,{"disambiguationData":[OSD([sQuery(id+"F8.wireOp",EDGE,"mOqyP8SL-vEXn-Shjf-BXRA-A4QvbKXMYqA2"),sQuery(id+"F8.wireOp",EDGE,"E5")])]});
            var Q30;
            {var subQ0=sQuery(id+"F15.wireOp",EDGE,"E24.bottom");Q30=makeQuery(id+"F16.boolean.opBoolean","COPY",EDGE,{"disambiguationData":[topologyDisambiguationEdgeConnected([makeQuery(id+"F9.opExtrude","SWEPT_FACE",FACE,{"disambiguationData":[OSD([sQuery(id+"F8.wireOp",EDGE,"E5")])]})])],"derivedFrom":makeQuery(id+"F16.opExtrude","CAP_EDGE",EDGE,{"disambiguationData":[OSD([subQ0])],"isStart":true})});}
            var Q31;
            {var subQ0=sQuery(id+"F15.wireOp",EDGE,"E24.bottom");Q31=makeQuery(id+"F16.boolean.opBoolean","COPY",EDGE,{"disambiguationData":[topologyDisambiguationEdgeConnected([makeQuery(id+"F10.opExtrude","SWEPT_FACE",FACE,{"disambiguationData":[OSD([sQuery(id+"F8.wireOp",EDGE,"E5")])]})])],"derivedFrom":makeQuery(id+"F16.opExtrude","CAP_EDGE",EDGE,{"disambiguationData":[OSD([subQ0])],"isStart":true})});}
            var Q32;
            {var subQ0=sQuery(id+"F15.wireOp",EDGE,"E24.top");Q32=makeQuery(id+"F16.boolean.opBoolean","COPY",EDGE,{"disambiguationData":[topologyDisambiguationEdgeConnected([makeQuery(id+"F9.opExtrude","SWEPT_FACE",FACE,{"disambiguationData":[OSD([sQuery(id+"F8.wireOp",EDGE,"E5")])]})])],"derivedFrom":makeQuery(id+"F16.opExtrude","CAP_EDGE",EDGE,{"disambiguationData":[OSD([subQ0])],"isStart":true})});}
            var Q33;
            {var subQ0=sQuery(id+"F15.wireOp",EDGE,"E24.top");Q33=makeQuery(id+"F16.boolean.opBoolean","COPY",EDGE,{"disambiguationData":[topologyDisambiguationEdgeConnected([makeQuery(id+"F10.opExtrude","SWEPT_FACE",FACE,{"disambiguationData":[OSD([sQuery(id+"F8.wireOp",EDGE,"E5")])]})])],"derivedFrom":makeQuery(id+"F16.opExtrude","CAP_EDGE",EDGE,{"disambiguationData":[OSD([subQ0])],"isStart":true})});}
            var Q34;
            Q34=makeQuery(id+"F9.opExtrude","SWEPT_EDGE",EDGE,{"disambiguationData":[OSD([sQuery(id+"F8.wireOp",EDGE,"Jx2hsfEg-rsGK-g6mN-gGwm-UTiYR1x8r5xO"),sQuery(id+"F8.wireOp",EDGE,"E5")])]});
            var Q35;
            Q35=makeQuery(id+"F10.opExtrude","SWEPT_EDGE",EDGE,{"disambiguationData":[OSD([sQuery(id+"F8.wireOp",EDGE,"Jx2hsfEg-rsGK-g6mN-gGwm-UTiYR1x8r5xO"),sQuery(id+"F8.wireOp",EDGE,"E5")])]});
            var Q36;
            Q36=makeQuery(id+"F9.opExtrude","SWEPT_EDGE",EDGE,{"disambiguationData":[OSD([sQuery(id+"F8.wireOp",EDGE,"7PxteJ0w-hNWy-X14L-V5LG-c6Ao6gPeCcrO"),sQuery(id+"F8.wireOp",EDGE,"Jx2hsfEg-rsGK-g6mN-gGwm-UTiYR1x8r5xO")])]});
            var Q37;
            Q37=makeQuery(id+"F10.opExtrude","SWEPT_EDGE",EDGE,{"disambiguationData":[OSD([sQuery(id+"F8.wireOp",EDGE,"7PxteJ0w-hNWy-X14L-V5LG-c6Ao6gPeCcrO"),sQuery(id+"F8.wireOp",EDGE,"Jx2hsfEg-rsGK-g6mN-gGwm-UTiYR1x8r5xO")])]});
            var Q38;
            Q38=makeQuery(id+"F9.opExtrude","SWEPT_EDGE",EDGE,{"disambiguationData":[OSD([sQuery(id+"F8.wireOp",EDGE,"4ElTsRrF-d6Ta-Xpu3-N1rJ-FU14qHi0ozwZ"),sQuery(id+"F8.wireOp",EDGE,"7PxteJ0w-hNWy-X14L-V5LG-c6Ao6gPeCcrO")])]});
            var Q39;
            Q39=makeQuery(id+"F10.opExtrude","SWEPT_EDGE",EDGE,{"disambiguationData":[OSD([sQuery(id+"F8.wireOp",EDGE,"4ElTsRrF-d6Ta-Xpu3-N1rJ-FU14qHi0ozwZ"),sQuery(id+"F8.wireOp",EDGE,"7PxteJ0w-hNWy-X14L-V5LG-c6Ao6gPeCcrO")])]});
            var Q40;
            Q40=makeQuery(id+"F10.opExtrude","SWEPT_EDGE",EDGE,{"disambiguationData":[OSD([sQuery(id+"F8.wireOp",EDGE,"E1"),sQuery(id+"F8.wireOp",EDGE,"4ElTsRrF-d6Ta-Xpu3-N1rJ-FU14qHi0ozwZ")])]});
            var Q41;
            Q41=makeQuery(id+"F9.opExtrude","SWEPT_EDGE",EDGE,{"disambiguationData":[OSD([sQuery(id+"F8.wireOp",EDGE,"E1"),sQuery(id+"F8.wireOp",EDGE,"4ElTsRrF-d6Ta-Xpu3-N1rJ-FU14qHi0ozwZ")])]});
            var Q42;
            Q42=makeQuery(id+"F9.opExtrude","SWEPT_EDGE",EDGE,{"disambiguationData":[OSD([sQuery(id+"F8.wireOp",EDGE,"E0"),sQuery(id+"F8.wireOp",EDGE,"E1")])]});
            var Q43;
            Q43=makeQuery(id+"F10.opExtrude","SWEPT_EDGE",EDGE,{"disambiguationData":[OSD([sQuery(id+"F8.wireOp",EDGE,"E0"),sQuery(id+"F8.wireOp",EDGE,"E1")])]});
            var Q44;
            Q44=makeQuery(id+"F10.opExtrude","SWEPT_EDGE",EDGE,{"disambiguationData":[OSD([sQuery(id+"F8.wireOp",EDGE,"E3"),sQuery(id+"F8.wireOp",EDGE,"E4")])]});
            var Q45;
            Q45=makeQuery(id+"F10.opExtrude","SWEPT_EDGE",EDGE,{"disambiguationData":[OSD([sQuery(id+"F8.wireOp",EDGE,"E4"),sQuery(id+"F8.wireOp",EDGE,"orgWuDI4-4pWB-4aS4-cs57-z0Hx2wF69UBw")])]});
            var Q46;
            Q46=makeQuery(id+"F9.opExtrude","SWEPT_EDGE",EDGE,{"disambiguationData":[OSD([sQuery(id+"F8.wireOp",EDGE,"E7"),sQuery(id+"F8.wireOp",EDGE,"E11")])]});
            var Q47;
            Q47=makeQuery(id+"F10.opExtrude","SWEPT_EDGE",EDGE,{"disambiguationData":[OSD([sQuery(id+"F8.wireOp",EDGE,"E7"),sQuery(id+"F8.wireOp",EDGE,"E11")])]});
            var Q48;
            Q48=makeQuery(id+"F10.opExtrude","SWEPT_EDGE",EDGE,{"disambiguationData":[OSD([sQuery(id+"F8.wireOp",EDGE,"E6"),sQuery(id+"F8.wireOp",EDGE,"E10")])]});
            var Q49;
            Q49=makeQuery(id+"F9.opExtrude","SWEPT_EDGE",EDGE,{"disambiguationData":[OSD([sQuery(id+"F8.wireOp",EDGE,"E6"),sQuery(id+"F8.wireOp",EDGE,"E10")])]});
            fillet(context, id + "F42", {"entities" : qUnion([Q0, Q1, Q2, Q3, Q4, Q5, Q6, Q7, Q8, Q9, Q10, Q11, Q12, Q13, Q14, Q15, Q16, Q17, Q18, Q19, Q20, Q21, Q22, Q23, Q24, Q25, Q26, Q27, Q28, Q29, Q30, Q31, Q32, Q33, Q34, Q35, Q36, Q37, Q38, Q39, Q40, Q41, Q42, Q43, Q44, Q45, Q46, Q47, Q48, Q49]), "radius" : getVariable(context, 'FilletRadius'), "tangentPropagation" : true, "allowEdgeOverflow" : false});
        }
        {
            var Q0;
            Q0=makeQuery(id+"F20.boolean.opBoolean","MERGE",FACE,{"derivedFrom":[makeQuery(id+"F10.opExtrude","SWEPT_FACE",FACE,{"disambiguationData":[OSD([sQuery(id+"F8.wireOp",EDGE,"E3")])]}),makeQuery(id+"F20.opExtrude","CAP_FACE",FACE,{"disambiguationData":[OSD([sQuery(id+"F19.wireOp",EDGE,"E31"),sQuery(id+"F19.wireOp",EDGE,"E33"),sQuery(id+"F19.wireOp",EDGE,"E34"),sQuery(id+"F19.wireOp",EDGE,"E35"),sQuery(id+"F19.wireOp",EDGE,"E36"),sQuery(id+"F19.wireOp",EDGE,"E37")])],"isStart":true})]});
            var sketch = newSketch(context, id + "F43", { "sketchPlane" : qUnion([Q0])});
            skCircle(sketch, "E116", {"center": v(-35.4, -13) * mm, "radius": 12.5 * mm});
            skSolve(sketch);
        }
        {
            var Q0;
            Q0 = qSketchRegion(id + "F43", true);
            extrude(context, id + "F44", {"entities" : qUnion([Q0]), "operationType" : NewBodyOperationType.REMOVE, "depth" : 15 * mm, "offsetDistance" : 25 * mm});
        }
        {
            var Q0;
            Q0=makeQuery(id+"F10.opExtrude","CAP_FACE",FACE,{"disambiguationData":[OSD([sQuery(id+"F8.wireOp",EDGE,"E0"),sQuery(id+"F8.wireOp",EDGE,"E1"),sQuery(id+"F8.wireOp",EDGE,"4ElTsRrF-d6Ta-Xpu3-N1rJ-FU14qHi0ozwZ"),sQuery(id+"F8.wireOp",EDGE,"7PxteJ0w-hNWy-X14L-V5LG-c6Ao6gPeCcrO"),sQuery(id+"F8.wireOp",EDGE,"Jx2hsfEg-rsGK-g6mN-gGwm-UTiYR1x8r5xO"),sQuery(id+"F8.wireOp",EDGE,"E2"),sQuery(id+"F8.wireOp",EDGE,"E3"),sQuery(id+"F8.wireOp",EDGE,"E4"),sQuery(id+"F8.wireOp",EDGE,"orgWuDI4-4pWB-4aS4-cs57-z0Hx2wF69UBw"),sQuery(id+"F8.wireOp",EDGE,"4i0MoKHX-XmxI-cSmD-P7XZ-JZizBw6dTzRK"),sQuery(id+"F8.wireOp",EDGE,"mOqyP8SL-vEXn-Shjf-BXRA-A4QvbKXMYqA2"),sQuery(id+"F8.wireOp",EDGE,"E5")])],"isStart":false});
            var sketch = newSketch(context, id + "F45", { "sketchPlane" : qUnion([Q0])});
            skCircle(sketch, "E117", {"center": v(-74.32, 65.5) * mm, "radius": 2.85 * mm});
            skCircle(sketch, "E118", {"center": v(-105.32, 65.5) * mm, "radius": 2.85 * mm});
            skCircle(sketch, "E119", {"center": v(-74.32, 34.5) * mm, "radius": 2.85 * mm});
            skCircle(sketch, "E120", {"center": v(-18.9, 85) * mm, "radius": 2.85 * mm});
            skCircle(sketch, "E121", {"center": v(-18.9, 15) * mm, "radius": 2.85 * mm});
            skSolve(sketch);
        }
        {
            var Q0;
            Q0 = qSketchRegion(id + "F45", true);
            extrude(context, id + "F46", {"entities" : qUnion([Q0]), "operationType" : NewBodyOperationType.REMOVE, "oppositeDirection" : true, "depth" : getVariable(context, 'M3HeadRecessDepth'), "offsetDistance" : 25 * mm});
        }
        {
            var Q0;
            Q0=qCreatedBy(makeId("Front.planeOp"),FACE);
            var sketch = newSketch(context, id + "F47", { "sketchPlane" : qUnion([Q0])});
            skLineSegment(sketch, "E122", {"start": v(16.54, 20.33) * mm, "end": v(16.54, 80.33) * mm});
            skLineSegment(sketch, "E123", {"start": v(26.54, 90.33) * mm, "end": v(26.54, 80.33) * mm});
            skLineSegment(sketch, "E124", {"start": v(26.54, 10.33) * mm, "end": v(26.54, 20.33) * mm});
            skLineSegment(sketch, "E125", {"start": v(26.54, 80.33) * mm, "end": v(71.54, 80.33) * mm});
            skLineSegment(sketch, "E126", {"start": v(71.54, 80.33) * mm, "end": v(71.54, 20.33) * mm});
            skLineSegment(sketch, "E127", {"start": v(71.54, 20.33) * mm, "end": v(26.54, 20.33) * mm});
            skLineSegment(sketch, "E128", {"start": v(16.54, 80.33) * mm, "end": v(16.54, 90.33) * mm});
            skLineSegment(sketch, "E129", {"start": v(16.54, 20.33) * mm, "end": v(16.54, 10.33) * mm});
            skLineSegment(sketch, "E130", {"start": v(16.54, 10.33) * mm, "end": v(26.54, 10.33) * mm});
            skLineSegment(sketch, "E131", {"start": v(26.54, 90.33) * mm, "end": v(16.54, 90.33) * mm});
            skLineSegment(sketch, "E132", {"start": v(71.54, 80.33) * mm, "end": v(71.54, 90.33) * mm});
            skLineSegment(sketch, "E133", {"start": v(71.54, 90.33) * mm, "end": v(61.54, 90.33) * mm});
            skLineSegment(sketch, "E134", {"start": v(61.54, 90.33) * mm, "end": v(61.54, 80.33) * mm});
            skLineSegment(sketch, "E135", {"start": v(71.54, 20.33) * mm, "end": v(71.54, 10.33) * mm});
            skLineSegment(sketch, "E136", {"start": v(71.54, 10.33) * mm, "end": v(61.54, 10.33) * mm});
            skLineSegment(sketch, "E137", {"start": v(61.54, 10.33) * mm, "end": v(61.54, 20.33) * mm});
            skSolve(sketch);
        }
        {
            var Q0;
            Q0 = qSketchRegion(id + "F47", true);
            extrude(context, id + "F48", {"entities" : qUnion([Q0]), "oppositeDirection" : true, "depth" : 7 * mm, "offsetDistance" : 25 * mm});
        }
        {
            var Q0;
            Q0 = qSketchRegion(id + "F47", true);
            extrude(context, id + "F49", {"entities" : qUnion([Q0]), "depth" : 7 * mm, "offsetDistance" : 25 * mm});
        }
        {
            var Q0;
            Q0=makeQuery(id+"F49.opExtrude","SWEPT_FACE",FACE,{"disambiguationData":[OSD([sQuery(id+"F47.wireOp",EDGE,"E122")])]});
            var sketch = newSketch(context, id + "F50", { "sketchPlane" : qUnion([Q0])});
            skLineSegment(sketch, "E138.bottom", {"start": v(-4, 42.83) * mm, "end": v(4, 42.83) * mm});
            skLineSegment(sketch, "E138.top", {"start": v(-4, 57.83) * mm, "end": v(4, 57.83) * mm});
            skLineSegment(sketch, "E138.left", {"start": v(-4, 42.83) * mm, "end": v(-4, 57.83) * mm});
            skLineSegment(sketch, "E138.right", {"start": v(4, 42.83) * mm, "end": v(4, 57.83) * mm});
            skSolve(sketch);
        }
        {
            var Q0;
            Q0 = qSketchRegion(id + "F50", true);
            extrude(context, id + "F51", {"entities" : qUnion([Q0]), "operationType" : NewBodyOperationType.REMOVE, "oppositeDirection" : true, "depth" : 60 * mm, "offsetDistance" : 25 * mm});
        }
        {
            var Q0;
            Q0=makeQuery(id+"F49.opExtrude","SWEPT_FACE",FACE,{"disambiguationData":[OSD([sQuery(id+"F47.wireOp",EDGE,"E122")])]});
            var sketch = newSketch(context, id + "F52", { "sketchPlane" : qUnion([Q0])});
            skCircle(sketch, "E139", {"center": v(0, 72.83) * mm, "radius": 4.1 * mm});
            skCircle(sketch, "E140", {"center": v(0, 27.83) * mm, "radius": 4.1 * mm});
            skSolve(sketch);
        }
        {
            var Q0;
            Q0 = qSketchRegion(id + "F52", true);
            extrude(context, id + "F53", {"entities" : qUnion([Q0]), "operationType" : NewBodyOperationType.REMOVE, "oppositeDirection" : true, "depth" : getVariable(context, 'RodHoleDepth'), "offsetDistance" : 25 * mm});
        }
        {
            var Q0;
            Q0=makeQuery(id+"F49.opExtrude","SWEPT_FACE",FACE,{"disambiguationData":[OSD([sQuery(id+"F47.wireOp",EDGE,"E125")])]});
            var sketch = newSketch(context, id + "F54", { "sketchPlane" : qUnion([Q0])});
            skPoint(sketch, "E141", {"position": v(38.04, -13) * mm});
            skCircle(sketch, "E142", {"center": v(38.04, -13) * mm, "radius": 5.2 * mm});
            skPoint(sketch, "E143", {"position": v(38.04, -24.5) * mm});
            skArc(sketch, "E144", {"start": v(38.04, -24.5) * mm, "mid": v(46.17, -21.13) * mm, "end": v(49.54, -13) * mm});
            skArc(sketch, "E145", {"start": v(38.04, -24.5) * mm, "mid": v(29.9, -21.13) * mm, "end": v(26.54, -13) * mm});
            skLineSegment(sketch, "E146", {"start": v(26.54, -13) * mm, "end": v(26.54, -7) * mm});
            skLineSegment(sketch, "E147", {"start": v(49.54, -13) * mm, "end": v(49.54, -7) * mm});
            skLineSegment(sketch, "E148", {"start": v(26.54, -7) * mm, "end": v(49.54, -7) * mm});
            skSolve(sketch);
        }
        {
            var Q0;
            Q0 = qSketchRegion(id + "F54", true);
            extrude(context, id + "F55", {"entities" : qUnion([Q0]), "operationType" : NewBodyOperationType.ADD, "oppositeDirection" : true, "depth" : 10 * mm, "offsetDistance" : 25 * mm});
        }
        {
            var Q0;
            Q0=makeQuery(id+"F55.boolean.opBoolean","MERGE",FACE,{"derivedFrom":[makeQuery(id+"F49.opExtrude","SWEPT_FACE",FACE,{"disambiguationData":[OSD([sQuery(id+"F47.wireOp",EDGE,"E125")])]}),makeQuery(id+"F55.opExtrude","CAP_FACE",FACE,{"disambiguationData":[OSD([sQuery(id+"F54.wireOp",EDGE,"E142"),sQuery(id+"F54.wireOp",EDGE,"E144"),sQuery(id+"F54.wireOp",EDGE,"E145"),sQuery(id+"F54.wireOp",EDGE,"E146"),sQuery(id+"F54.wireOp",EDGE,"E147"),sQuery(id+"F54.wireOp",EDGE,"Y9nMjFpE-nWOr-VpX3-e2AY-2DFmD9UunTTT"),sQuery(id+"F54.wireOp",EDGE,"lLlcIz7O-eRHL-gcqc-swPK-21WdanJ8aFBY"),sQuery(id+"F54.wireOp",EDGE,"ZlSBgN9d-m597-jkxP-AhAW-4RFAAkR0QPYH")])],"isStart":true})]});
            var sketch = newSketch(context, id + "F56", { "sketchPlane" : qUnion([Q0])});
            skPoint(sketch, "E149", {"position": v(38.04, -13) * mm});
            skLineSegment(sketch, "E150", {"start": v(38.04, -13) * mm, "end": v(38.04, -5) * mm});
            skLineSegment(sketch, "E151", {"start": v(38.04, -13) * mm, "end": v(32.38, -7.34) * mm});
            skLineSegment(sketch, "E152", {"start": v(38.04, -13) * mm, "end": v(43.7, -18.66) * mm});
            skCircle(sketch, "E153", {"center": v(32.38, -7.34) * mm, "radius": 1.7 * mm});
            skCircle(sketch, "E154", {"center": v(43.7, -18.66) * mm, "radius": 1.7 * mm});
            skSolve(sketch);
        }
        {
            var Q0;
            Q0 = qSketchRegion(id + "F56", true);
            extrude(context, id + "F57", {"entities" : qUnion([Q0]), "operationType" : NewBodyOperationType.REMOVE, "oppositeDirection" : true, "depth" : 12.5 * mm, "offsetDistance" : 25 * mm});
        }
        {
            var Q0;
            Q0=makeQuery(id+"F55.opExtrude","CAP_FACE",FACE,{"disambiguationData":[OSD([sQuery(id+"F54.wireOp",EDGE,"E142"),sQuery(id+"F54.wireOp",EDGE,"E144"),sQuery(id+"F54.wireOp",EDGE,"E145"),sQuery(id+"F54.wireOp",EDGE,"E146"),sQuery(id+"F54.wireOp",EDGE,"E147"),sQuery(id+"F54.wireOp",EDGE,"E148")])],"isStart":false});
            var sketch = newSketch(context, id + "F58", { "sketchPlane" : qUnion([Q0])});
            skPoint(sketch, "E155", {"position": v(38.04, 13) * mm});
            skLineSegment(sketch, "E156", {"start": v(38.04, 13) * mm, "end": v(43.7, 18.66) * mm});
            skLineSegment(sketch, "E157", {"start": v(38.04, 13) * mm, "end": v(32.38, 7.34) * mm});
            skCircle(sketch, "E158.cCircle", {"center": v(43.7, 18.66) * mm, "radius": 2.8 * mm, "construction": true});
            skLineSegment(sketch, "E158.0", {"start": v(42.86, 15.53) * mm, "end": v(40.58, 17.82) * mm});
            skLineSegment(sketch, "E158.1", {"start": v(40.58, 17.82) * mm, "end": v(41.41, 20.94) * mm});
            skLineSegment(sketch, "E158.2", {"start": v(41.41, 20.94) * mm, "end": v(44.54, 21.78) * mm});
            skLineSegment(sketch, "E158.3", {"start": v(44.54, 21.78) * mm, "end": v(46.82, 19.5) * mm});
            skLineSegment(sketch, "E158.4", {"start": v(46.82, 19.5) * mm, "end": v(45.98, 16.37) * mm});
            skLineSegment(sketch, "E158.5", {"start": v(45.98, 16.37) * mm, "end": v(42.86, 15.53) * mm});
            skPoint(sketch, "E158.0.midPoint", {"position": v(41.72, 16.68) * mm});
            skCircle(sketch, "E159.cCircle", {"center": v(32.38, 7.34) * mm, "radius": 2.8 * mm, "construction": true});
            skLineSegment(sketch, "E159.0", {"start": v(33.22, 10.47) * mm, "end": v(35.5, 8.18) * mm});
            skLineSegment(sketch, "E159.1", {"start": v(35.5, 8.18) * mm, "end": v(34.67, 5.06) * mm});
            skLineSegment(sketch, "E159.2", {"start": v(34.67, 5.06) * mm, "end": v(31.55, 4.22) * mm});
            skLineSegment(sketch, "E159.3", {"start": v(31.55, 4.22) * mm, "end": v(29.26, 6.5) * mm});
            skLineSegment(sketch, "E159.4", {"start": v(29.26, 6.5) * mm, "end": v(30.1, 9.63) * mm});
            skLineSegment(sketch, "E159.5", {"start": v(30.1, 9.63) * mm, "end": v(33.22, 10.47) * mm});
            skPoint(sketch, "E159.0.midPoint", {"position": v(34.36, 9.32) * mm});
            skLineSegment(sketch, "E160", {"start": v(35.5, 8.18) * mm, "end": v(35.77, 9.15) * mm});
            skLineSegment(sketch, "E161", {"start": v(33.22, 10.47) * mm, "end": v(34.19, 10.72) * mm});
            skLineSegment(sketch, "E162", {"start": v(35.77, 9.15) * mm, "end": v(34.19, 10.72) * mm});
            skLineSegment(sketch, "E163", {"start": v(42.86, 15.53) * mm, "end": v(41.9, 15.28) * mm});
            skLineSegment(sketch, "E164", {"start": v(40.58, 17.82) * mm, "end": v(40.32, 16.85) * mm});
            skLineSegment(sketch, "E165", {"start": v(40.32, 16.85) * mm, "end": v(41.9, 15.28) * mm});
            skSolve(sketch);
        }
        {
            var Q0;
            Q0 = qSketchRegion(id + "F58", true);
            extrude(context, id + "F59", {"entities" : qUnion([Q0]), "operationType" : NewBodyOperationType.REMOVE, "oppositeDirection" : true, "depth" : getVariable(context, 'M3HexNutDepth'), "offsetDistance" : 25 * mm});
        }
        {
            var Q0;
            Q0 = qSketchRegion(id + "F58", true);
            extrude(context, id + "F60", {"entities" : qUnion([Q0]), "operationType" : NewBodyOperationType.REMOVE, "depth" : 10 * mm, "offsetDistance" : 25 * mm});
        }
        {
            var Q0;
            Q0=makeQuery(id+"F49.opExtrude","SWEPT_FACE",FACE,{"disambiguationData":[OSD([sQuery(id+"F47.wireOp",EDGE,"E127")])]});
            var sketch = newSketch(context, id + "F61", { "sketchPlane" : qUnion([Q0])});
            skPoint(sketch, "E166", {"position": v(38.04, 7) * mm});
            skPoint(sketch, "E167", {"position": v(38.04, 13) * mm});
            skPoint(sketch, "E168", {"position": v(55.04, 13) * mm});
            skArc(sketch, "E169", {"start": v(62.64, 13) * mm, "mid": v(55.04, 5.4) * mm, "end": v(47.44, 13) * mm});
            skLineSegment(sketch, "E170", {"start": v(62.64, 13) * mm, "end": v(47.44, 13) * mm});
            skSolve(sketch);
        }
        {
            var Q0;
            Q0 = qSketchRegion(id + "F61", true);
            extrude(context, id + "F62", {"entities" : qUnion([Q0]), "operationType" : NewBodyOperationType.REMOVE, "oppositeDirection" : true, "depth" : 46 * mm, "offsetDistance" : 25 * mm});
        }
        {
            var Q0;
            Q0=makeQuery(id+"F49.opExtrude","SWEPT_FACE",FACE,{"disambiguationData":[OSD([sQuery(id+"F47.wireOp",EDGE,"E127")])]});
            var sketch = newSketch(context, id + "F63", { "sketchPlane" : qUnion([Q0])});
            skPoint(sketch, "E171", {"position": v(55.04, 13) * mm});
            skArc(sketch, "E172", {"start": v(62.64, 13) * mm, "mid": v(55.04, 5.4) * mm, "end": v(47.44, 13) * mm});
            skLineSegment(sketch, "E173", {"start": v(62.64, 13) * mm, "end": v(67.4, 13) * mm});
            skLineSegment(sketch, "E174", {"start": v(47.44, 13) * mm, "end": v(42.7, 13) * mm});
            skLineSegment(sketch, "E175", {"start": v(67.4, 13) * mm, "end": v(67.4, 5) * mm});
            skLineSegment(sketch, "E176", {"start": v(42.7, 13) * mm, "end": v(42.7, 5) * mm});
            skLineSegment(sketch, "E177", {"start": v(42.7, 5) * mm, "end": v(67.4, 5) * mm});
            skSolve(sketch);
        }
        {
            var Q0;
            Q0 = qSketchRegion(id + "F63", true);
            extrude(context, id + "F64", {"entities" : qUnion([Q0]), "operationType" : NewBodyOperationType.ADD, "oppositeDirection" : true, "depth" : 5 * mm + getVariable(context, 'Tolerance') / 2, "offsetDistance" : 25 * mm});
        }
        {
            var Q0;
            {var subQ0=sQuery(id+"F63.wireOp",EDGE,"E174");var subQ1=sQuery(id+"F63.wireOp",EDGE,"E172");var subQ2=sQuery(id+"F63.wireOp",EDGE,"E176");Q0=makeQuery(id+"F64.boolean.opBoolean","SPLIT",FACE,{"disambiguationData":[TD([makeQuery(id+"F64.opExtrude","SWEPT_FACE",FACE,{"disambiguationData":[OSD([subQ0])]})])],"derivedFrom":makeQuery(id+"F64.opExtrude","CAP_FACE",FACE,{"disambiguationData":[OSD([subQ1,sQuery(id+"F63.wireOp",EDGE,"E173"),subQ0,sQuery(id+"F63.wireOp",EDGE,"E175"),subQ2,sQuery(id+"F63.wireOp",EDGE,"E177")])],"isStart":false})});}
            var sketch = newSketch(context, id + "F65", { "sketchPlane" : qUnion([Q0])});
            skPoint(sketch, "E178", {"position": v(55.04, -13) * mm});
            skArc(sketch, "E179", {"start": v(47.8, -13) * mm, "mid": v(55.04, -5.75) * mm, "end": v(62.3, -13) * mm});
            skLineSegment(sketch, "E180", {"start": v(47.8, -13) * mm, "end": v(42.7, -13) * mm});
            skLineSegment(sketch, "E181", {"start": v(62.3, -13) * mm, "end": v(67.4, -13) * mm});
            skLineSegment(sketch, "E182", {"start": v(67.4, -13) * mm, "end": v(67.4, -5) * mm});
            skLineSegment(sketch, "E183", {"start": v(42.7, -13) * mm, "end": v(42.7, -5) * mm});
            skLineSegment(sketch, "E184", {"start": v(67.4, -5) * mm, "end": v(42.7, -5) * mm});
            skSolve(sketch);
        }
        {
            var Q0;
            Q0 = qSketchRegion(id + "F65", true);
            extrude(context, id + "F66", {"entities" : qUnion([Q0]), "operationType" : NewBodyOperationType.ADD, "depth" : 1.1 * mm - getVariable(context, 'Tolerance'), "offsetDistance" : 25 * mm});
        }
        {
            var Q0;
            Q0=makeQuery(id+"F66.opExtrude","CAP_FACE",FACE,{"disambiguationData":[OSD([sQuery(id+"F65.wireOp",EDGE,"E179"),sQuery(id+"F65.wireOp",EDGE,"E180"),sQuery(id+"F65.wireOp",EDGE,"E181"),sQuery(id+"F65.wireOp",EDGE,"E182"),sQuery(id+"F65.wireOp",EDGE,"E183"),sQuery(id+"F65.wireOp",EDGE,"E184")])],"isStart":false});
            var sketch = newSketch(context, id + "F67", { "sketchPlane" : qUnion([Q0])});
            skPoint(sketch, "E185", {"position": v(55.04, -13) * mm});
            skArc(sketch, "E186", {"start": v(62.64, -13) * mm, "mid": v(55.04, -5.4) * mm, "end": v(47.44, -13) * mm});
            skLineSegment(sketch, "E187", {"start": v(62.64, -13) * mm, "end": v(67.4, -13) * mm});
            skLineSegment(sketch, "E188", {"start": v(67.4, -13) * mm, "end": v(67.4, -5) * mm});
            skLineSegment(sketch, "E189", {"start": v(47.44, -13) * mm, "end": v(42.7, -13) * mm});
            skLineSegment(sketch, "E190", {"start": v(42.7, -13) * mm, "end": v(42.7, -5) * mm});
            skLineSegment(sketch, "E191", {"start": v(67.4, -5) * mm, "end": v(42.7, -5) * mm});
            skSolve(sketch);
        }
        {
            var Q0;
            Q0 = qSketchRegion(id + "F67", true);
            extrude(context, id + "F68", {"entities" : qUnion([Q0]), "operationType" : NewBodyOperationType.ADD, "depth" : 32.8 * mm + getVariable(context, 'Tolerance'), "offsetDistance" : 25 * mm});
        }
        {
            var Q0;
            {var subQ0=sQuery(id+"F67.wireOp",EDGE,"E189");var subQ1=sQuery(id+"F67.wireOp",EDGE,"E186");var subQ2=sQuery(id+"F67.wireOp",EDGE,"E190");Q0=makeQuery(id+"F68.boolean.opBoolean","SPLIT",FACE,{"disambiguationData":[TD([makeQuery(id+"F64.opExtrude","SWEPT_FACE",FACE,{"disambiguationData":[OSD([sQuery(id+"F63.wireOp",EDGE,"E174")])]})])],"derivedFrom":makeQuery(id+"F68.opExtrude","CAP_FACE",FACE,{"disambiguationData":[OSD([subQ1,sQuery(id+"F67.wireOp",EDGE,"E187"),sQuery(id+"F67.wireOp",EDGE,"E188"),subQ0,subQ2,sQuery(id+"F67.wireOp",EDGE,"E191")])],"isStart":false})});}
            var sketch = newSketch(context, id + "F69", { "sketchPlane" : qUnion([Q0])});
            skPoint(sketch, "E192", {"position": v(55.04, -13) * mm});
            skArc(sketch, "E193", {"start": v(47.8, -13) * mm, "mid": v(55.04, -5.75) * mm, "end": v(62.3, -13) * mm});
            skLineSegment(sketch, "E194", {"start": v(47.8, -13) * mm, "end": v(42.7, -13) * mm});
            skLineSegment(sketch, "E195", {"start": v(42.7, -13) * mm, "end": v(42.7, -5) * mm});
            skLineSegment(sketch, "E196", {"start": v(62.3, -13) * mm, "end": v(67.4, -13) * mm});
            skLineSegment(sketch, "E197", {"start": v(67.4, -13) * mm, "end": v(67.4, -5) * mm});
            skLineSegment(sketch, "E198", {"start": v(42.7, -5) * mm, "end": v(67.4, -5) * mm});
            skSolve(sketch);
        }
        {
            var Q0;
            Q0 = qSketchRegion(id + "F69", true);
            extrude(context, id + "F70", {"entities" : qUnion([Q0]), "operationType" : NewBodyOperationType.ADD, "depth" : 1.1 * mm - getVariable(context, 'Tolerance'), "offsetDistance" : 25 * mm});
        }
        {
            var Q0;
            Q0=makeQuery(id+"F70.opExtrude","CAP_FACE",FACE,{"disambiguationData":[OSD([sQuery(id+"F69.wireOp",EDGE,"E193"),sQuery(id+"F69.wireOp",EDGE,"E194"),sQuery(id+"F69.wireOp",EDGE,"E195"),sQuery(id+"F69.wireOp",EDGE,"E196"),sQuery(id+"F69.wireOp",EDGE,"E197"),sQuery(id+"F69.wireOp",EDGE,"E198")])],"isStart":false});
            var sketch = newSketch(context, id + "F71", { "sketchPlane" : qUnion([Q0])});
            skPoint(sketch, "E199", {"position": v(55.04, -13) * mm});
            skArc(sketch, "E200", {"start": v(62.64, -13) * mm, "mid": v(55.04, -5.4) * mm, "end": v(47.44, -13) * mm});
            skLineSegment(sketch, "E201", {"start": v(62.64, -13) * mm, "end": v(67.4, -13) * mm});
            skLineSegment(sketch, "E202", {"start": v(67.4, -13) * mm, "end": v(67.4, -7) * mm});
            skLineSegment(sketch, "E203", {"start": v(47.44, -13) * mm, "end": v(42.7, -13) * mm});
            skLineSegment(sketch, "E204", {"start": v(42.7, -13) * mm, "end": v(42.7, -7) * mm});
            skLineSegment(sketch, "E205", {"start": v(42.7, -7) * mm, "end": v(42.7, -5) * mm});
            skLineSegment(sketch, "E206", {"start": v(67.4, -7) * mm, "end": v(67.4, -5) * mm});
            skLineSegment(sketch, "E207", {"start": v(42.7, -5) * mm, "end": v(67.4, -5) * mm});
            skSolve(sketch);
        }
        {
            var Q0;
            Q0 = qSketchRegion(id + "F71", true);
            extrude(context, id + "F72", {"entities" : qUnion([Q0]), "operationType" : NewBodyOperationType.ADD, "depth" : 5 * mm + getVariable(context, 'Tolerance') / 2, "offsetDistance" : 25 * mm});
        }
        {
            var Q0;
            Q0=makeQuery(id+"F49.opExtrude","CAP_FACE",FACE,{"disambiguationData":[OSD([sQuery(id+"F47.wireOp",EDGE,"E122"),sQuery(id+"F47.wireOp",EDGE,"vHFABqv0-Ybvm-PYqP-B5kJ-UVV6UIBHEKYA"),sQuery(id+"F47.wireOp",EDGE,"80JhjZWx-GQqo-LaVo-pp9a-fqlwG0YZ1vDd"),sQuery(id+"F47.wireOp",EDGE,"qFPor4tA-krSn-UBEH-swcX-wpI3ccUzTAWm"),sQuery(id+"F47.wireOp",EDGE,"40H9p0Nx-gS3a-jbsE-J0sd-cglVmnDpoqKR"),sQuery(id+"F47.wireOp",EDGE,"c1tvB95E-VLiR-0DcJ-Cz1R-gRm9P8e078v8"),sQuery(id+"F47.wireOp",EDGE,"20FqZ1HW-nhpa-fodr-DXJK-6u80PBLsJZi3"),sQuery(id+"F47.wireOp",EDGE,"E123"),sQuery(id+"F47.wireOp",EDGE,"E124"),sQuery(id+"F47.wireOp",EDGE,"E125"),sQuery(id+"F47.wireOp",EDGE,"E126"),sQuery(id+"F47.wireOp",EDGE,"E127")])],"isStart":false});
            var sketch = newSketch(context, id + "F73", { "sketchPlane" : qUnion([Q0])});
            skCircle(sketch, "E208", {"center": v(21.54, 85.33) * mm, "radius": 1.7 * mm});
            skPoint(sketch, "E208.centerSnap0", {"position": v(26.54, 85.33) * mm});
            skPoint(sketch, "E208.centerSnap1", {"position": v(21.54, 90.33) * mm});
            skCircle(sketch, "E209", {"center": v(21.54, 15.33) * mm, "radius": 1.7 * mm});
            skPoint(sketch, "E209.centerSnap0", {"position": v(21.54, 10.33) * mm});
            skPoint(sketch, "E209.centerSnap1", {"position": v(26.54, 15.33) * mm});
            skCircle(sketch, "E210", {"center": v(66.54, 85.33) * mm, "radius": 1.7 * mm});
            skPoint(sketch, "E210.centerSnap0", {"position": v(61.54, 85.33) * mm});
            skPoint(sketch, "E210.centerSnap1", {"position": v(66.54, 90.33) * mm});
            skCircle(sketch, "E211", {"center": v(66.54, 15.33) * mm, "radius": 1.7 * mm});
            skPoint(sketch, "E211.centerSnap0", {"position": v(66.54, 10.33) * mm});
            skPoint(sketch, "E211.centerSnap1", {"position": v(61.54, 15.33) * mm});
            skSolve(sketch);
        }
        {
            var Q0;
            Q0 = qSketchRegion(id + "F73", true);
            extrude(context, id + "F74", {"entities" : qUnion([Q0]), "operationType" : NewBodyOperationType.REMOVE, "oppositeDirection" : true, "depth" : 25 * mm, "offsetDistance" : 25 * mm});
        }
        {
            var Q0;
            Q0=makeQuery(id+"F72.boolean.opBoolean","MERGE",FACE,{"derivedFrom":[makeQuery(id+"F70.boolean.opBoolean","MERGE",FACE,{"derivedFrom":[makeQuery(id+"F68.boolean.opBoolean","MERGE",FACE,{"derivedFrom":[makeQuery(id+"F66.boolean.opBoolean","MERGE",FACE,{"derivedFrom":[makeQuery(id+"F64.opExtrude","SWEPT_FACE",FACE,{"disambiguationData":[OSD([sQuery(id+"F63.wireOp",EDGE,"E174")])]}),makeQuery(id+"F66.opExtrude","SWEPT_FACE",FACE,{"disambiguationData":[OSD([sQuery(id+"F65.wireOp",EDGE,"E180")])]})]}),makeQuery(id+"F68.opExtrude","SWEPT_FACE",FACE,{"disambiguationData":[OSD([sQuery(id+"F67.wireOp",EDGE,"E189")])]})]}),makeQuery(id+"F70.opExtrude","SWEPT_FACE",FACE,{"disambiguationData":[OSD([sQuery(id+"F69.wireOp",EDGE,"E194")])]})]}),makeQuery(id+"F72.opExtrude","SWEPT_FACE",FACE,{"disambiguationData":[OSD([sQuery(id+"F71.wireOp",EDGE,"D6DGubul-URO0-qaXw-Zher-GUvIj9uJXMxI")])]})]});
            var sketch = newSketch(context, id + "F75", { "sketchPlane" : qUnion([Q0])});
            skPoint(sketch, "E212", {"position": v(45.2, 62.83) * mm});
            skPoint(sketch, "E213", {"position": v(45.2, 36.83) * mm});
            skCircle(sketch, "E214", {"center": v(45.2, 62.83) * mm, "radius": 1.7 * mm});
            skCircle(sketch, "E215", {"center": v(45.2, 36.83) * mm, "radius": 1.7 * mm});
            skPoint(sketch, "E216", {"position": v(64.9, 62.83) * mm});
            skPoint(sketch, "E217", {"position": v(64.9, 36.83) * mm});
            skCircle(sketch, "E218", {"center": v(64.9, 62.83) * mm, "radius": 1.7 * mm});
            skCircle(sketch, "E219", {"center": v(64.9, 36.83) * mm, "radius": 1.7 * mm});
            skSolve(sketch);
        }
        {
            var Q0;
            Q0 = qSketchRegion(id + "F75", true);
            extrude(context, id + "F76", {"entities" : qUnion([Q0]), "operationType" : NewBodyOperationType.REMOVE, "oppositeDirection" : true, "depth" : 20 * mm, "offsetDistance" : 25 * mm});
        }
        {
            var Q0;
            Q0=makeQuery(id+"F48.opExtrude","CAP_FACE",FACE,{"disambiguationData":[OSD([sQuery(id+"F47.wireOp",EDGE,"E122"),sQuery(id+"F47.wireOp",EDGE,"vHFABqv0-Ybvm-PYqP-B5kJ-UVV6UIBHEKYA"),sQuery(id+"F47.wireOp",EDGE,"80JhjZWx-GQqo-LaVo-pp9a-fqlwG0YZ1vDd"),sQuery(id+"F47.wireOp",EDGE,"qFPor4tA-krSn-UBEH-swcX-wpI3ccUzTAWm"),sQuery(id+"F47.wireOp",EDGE,"40H9p0Nx-gS3a-jbsE-J0sd-cglVmnDpoqKR"),sQuery(id+"F47.wireOp",EDGE,"c1tvB95E-VLiR-0DcJ-Cz1R-gRm9P8e078v8"),sQuery(id+"F47.wireOp",EDGE,"20FqZ1HW-nhpa-fodr-DXJK-6u80PBLsJZi3"),sQuery(id+"F47.wireOp",EDGE,"E123"),sQuery(id+"F47.wireOp",EDGE,"E124"),sQuery(id+"F47.wireOp",EDGE,"E125"),sQuery(id+"F47.wireOp",EDGE,"E126"),sQuery(id+"F47.wireOp",EDGE,"E127")])],"isStart":false});
            var sketch = newSketch(context, id + "F77", { "sketchPlane" : qUnion([Q0])});
            skCircle(sketch, "E220.cCircle", {"center": v(-21.54, 85.33) * mm, "radius": 2.8 * mm, "construction": true});
            skLineSegment(sketch, "E220.0", {"start": v(-23.16, 88.13) * mm, "end": v(-19.93, 88.13) * mm});
            skLineSegment(sketch, "E220.1", {"start": v(-19.93, 88.13) * mm, "end": v(-18.3, 85.33) * mm});
            skLineSegment(sketch, "E220.2", {"start": v(-18.3, 85.33) * mm, "end": v(-19.93, 82.53) * mm});
            skLineSegment(sketch, "E220.3", {"start": v(-19.93, 82.53) * mm, "end": v(-23.16, 82.53) * mm});
            skLineSegment(sketch, "E220.4", {"start": v(-23.16, 82.53) * mm, "end": v(-24.77, 85.33) * mm});
            skLineSegment(sketch, "E220.5", {"start": v(-24.77, 85.33) * mm, "end": v(-23.16, 88.13) * mm});
            skPoint(sketch, "E220.0.midPoint", {"position": v(-21.54, 88.13) * mm});
            skCircle(sketch, "E221.cCircle", {"center": v(-21.54, 15.33) * mm, "radius": 2.8 * mm, "construction": true});
            skLineSegment(sketch, "E221.0", {"start": v(-23.16, 18.13) * mm, "end": v(-19.93, 18.13) * mm});
            skLineSegment(sketch, "E221.1", {"start": v(-19.93, 18.13) * mm, "end": v(-18.3, 15.33) * mm});
            skLineSegment(sketch, "E221.2", {"start": v(-18.3, 15.33) * mm, "end": v(-19.93, 12.53) * mm});
            skLineSegment(sketch, "E221.3", {"start": v(-19.93, 12.53) * mm, "end": v(-23.16, 12.53) * mm});
            skLineSegment(sketch, "E221.4", {"start": v(-23.16, 12.53) * mm, "end": v(-24.77, 15.33) * mm});
            skLineSegment(sketch, "E221.5", {"start": v(-24.77, 15.33) * mm, "end": v(-23.16, 18.13) * mm});
            skPoint(sketch, "E221.0.midPoint", {"position": v(-21.54, 18.13) * mm});
            skCircle(sketch, "E222.cCircle", {"center": v(-66.54, 15.33) * mm, "radius": 2.8 * mm, "construction": true});
            skLineSegment(sketch, "E222.0", {"start": v(-68.16, 18.13) * mm, "end": v(-64.93, 18.13) * mm});
            skLineSegment(sketch, "E222.1", {"start": v(-64.93, 18.13) * mm, "end": v(-63.3, 15.33) * mm});
            skLineSegment(sketch, "E222.2", {"start": v(-63.3, 15.33) * mm, "end": v(-64.93, 12.53) * mm});
            skLineSegment(sketch, "E222.3", {"start": v(-64.93, 12.53) * mm, "end": v(-68.16, 12.53) * mm});
            skLineSegment(sketch, "E222.4", {"start": v(-68.16, 12.53) * mm, "end": v(-69.77, 15.33) * mm});
            skLineSegment(sketch, "E222.5", {"start": v(-69.77, 15.33) * mm, "end": v(-68.16, 18.13) * mm});
            skPoint(sketch, "E222.0.midPoint", {"position": v(-66.54, 18.13) * mm});
            skCircle(sketch, "E223.cCircle", {"center": v(-66.54, 85.33) * mm, "radius": 2.8 * mm, "construction": true});
            skLineSegment(sketch, "E223.0", {"start": v(-68.16, 88.13) * mm, "end": v(-64.93, 88.13) * mm});
            skLineSegment(sketch, "E223.1", {"start": v(-64.93, 88.13) * mm, "end": v(-63.3, 85.33) * mm});
            skLineSegment(sketch, "E223.2", {"start": v(-63.3, 85.33) * mm, "end": v(-64.93, 82.53) * mm});
            skLineSegment(sketch, "E223.3", {"start": v(-64.93, 82.53) * mm, "end": v(-68.16, 82.53) * mm});
            skLineSegment(sketch, "E223.4", {"start": v(-68.16, 82.53) * mm, "end": v(-69.77, 85.33) * mm});
            skLineSegment(sketch, "E223.5", {"start": v(-69.77, 85.33) * mm, "end": v(-68.16, 88.13) * mm});
            skPoint(sketch, "E223.0.midPoint", {"position": v(-66.54, 88.13) * mm});
            skCircle(sketch, "E224.cCircle", {"center": v(-64.9, 62.83) * mm, "radius": 2.8 * mm, "construction": true});
            skLineSegment(sketch, "E224.0", {"start": v(-66.5, 65.63) * mm, "end": v(-63.28, 65.63) * mm});
            skLineSegment(sketch, "E224.1", {"start": v(-63.28, 65.63) * mm, "end": v(-61.66, 62.83) * mm});
            skLineSegment(sketch, "E224.2", {"start": v(-61.66, 62.83) * mm, "end": v(-63.28, 60.03) * mm});
            skLineSegment(sketch, "E224.3", {"start": v(-63.28, 60.03) * mm, "end": v(-66.5, 60.03) * mm});
            skLineSegment(sketch, "E224.4", {"start": v(-66.5, 60.03) * mm, "end": v(-68.12, 62.83) * mm});
            skLineSegment(sketch, "E224.5", {"start": v(-68.12, 62.83) * mm, "end": v(-66.5, 65.63) * mm});
            skPoint(sketch, "E224.0.midPoint", {"position": v(-64.9, 65.63) * mm});
            skCircle(sketch, "E225.cCircle", {"center": v(-45.2, 62.83) * mm, "radius": 2.8 * mm, "construction": true});
            skLineSegment(sketch, "E225.0", {"start": v(-46.8, 65.63) * mm, "end": v(-43.58, 65.63) * mm});
            skLineSegment(sketch, "E225.1", {"start": v(-43.58, 65.63) * mm, "end": v(-41.96, 62.83) * mm});
            skLineSegment(sketch, "E225.2", {"start": v(-41.96, 62.83) * mm, "end": v(-43.58, 60.03) * mm});
            skLineSegment(sketch, "E225.3", {"start": v(-43.58, 60.03) * mm, "end": v(-46.8, 60.03) * mm});
            skLineSegment(sketch, "E225.4", {"start": v(-46.8, 60.03) * mm, "end": v(-48.42, 62.83) * mm});
            skLineSegment(sketch, "E225.5", {"start": v(-48.42, 62.83) * mm, "end": v(-46.8, 65.63) * mm});
            skPoint(sketch, "E225.0.midPoint", {"position": v(-45.2, 65.63) * mm});
            skCircle(sketch, "E226.cCircle", {"center": v(-45.2, 36.83) * mm, "radius": 2.8 * mm, "construction": true});
            skLineSegment(sketch, "E226.0", {"start": v(-46.8, 39.63) * mm, "end": v(-43.58, 39.63) * mm});
            skLineSegment(sketch, "E226.1", {"start": v(-43.58, 39.63) * mm, "end": v(-41.96, 36.83) * mm});
            skLineSegment(sketch, "E226.2", {"start": v(-41.96, 36.83) * mm, "end": v(-43.58, 34.03) * mm});
            skLineSegment(sketch, "E226.3", {"start": v(-43.58, 34.03) * mm, "end": v(-46.8, 34.03) * mm});
            skLineSegment(sketch, "E226.4", {"start": v(-46.8, 34.03) * mm, "end": v(-48.42, 36.83) * mm});
            skLineSegment(sketch, "E226.5", {"start": v(-48.42, 36.83) * mm, "end": v(-46.8, 39.63) * mm});
            skPoint(sketch, "E226.0.midPoint", {"position": v(-45.2, 39.63) * mm});
            skCircle(sketch, "E227.cCircle", {"center": v(-64.9, 36.83) * mm, "radius": 2.8 * mm, "construction": true});
            skLineSegment(sketch, "E227.0", {"start": v(-66.5, 39.63) * mm, "end": v(-63.28, 39.63) * mm});
            skLineSegment(sketch, "E227.1", {"start": v(-63.28, 39.63) * mm, "end": v(-61.66, 36.83) * mm});
            skLineSegment(sketch, "E227.2", {"start": v(-61.66, 36.83) * mm, "end": v(-63.28, 34.03) * mm});
            skLineSegment(sketch, "E227.3", {"start": v(-63.28, 34.03) * mm, "end": v(-66.5, 34.03) * mm});
            skLineSegment(sketch, "E227.4", {"start": v(-66.5, 34.03) * mm, "end": v(-68.12, 36.83) * mm});
            skLineSegment(sketch, "E227.5", {"start": v(-68.12, 36.83) * mm, "end": v(-66.5, 39.63) * mm});
            skPoint(sketch, "E227.0.midPoint", {"position": v(-64.9, 39.63) * mm});
            skSolve(sketch);
        }
        {
            var Q0;
            Q0 = qSketchRegion(id + "F77", true);
            extrude(context, id + "F78", {"entities" : qUnion([Q0]), "operationType" : NewBodyOperationType.REMOVE, "oppositeDirection" : true, "depth" : getVariable(context, 'M3HexNutDepth'), "offsetDistance" : 25 * mm});
        }
        {
            var Q0;
            Q0=makeQuery(id+"F49.opExtrude","SWEPT_EDGE",EDGE,{"disambiguationData":[OSD([sQuery(id+"F47.wireOp",EDGE,"E123"),sQuery(id+"F47.wireOp",EDGE,"E125")])]});
            var Q1;
            Q1=makeQuery(id+"F48.opExtrude","SWEPT_EDGE",EDGE,{"disambiguationData":[OSD([sQuery(id+"F47.wireOp",EDGE,"E123"),sQuery(id+"F47.wireOp",EDGE,"E125")])]});
            var Q2;
            Q2=makeQuery(id+"F49.opExtrude","SWEPT_EDGE",EDGE,{"disambiguationData":[OSD([sQuery(id+"F47.wireOp",EDGE,"E125"),sQuery(id+"F47.wireOp",EDGE,"E126")])]});
            var Q3;
            Q3=makeQuery(id+"F48.opExtrude","SWEPT_EDGE",EDGE,{"disambiguationData":[OSD([sQuery(id+"F47.wireOp",EDGE,"E125"),sQuery(id+"F47.wireOp",EDGE,"E126")])]});
            var Q4;
            Q4=makeQuery(id+"F49.opExtrude","SWEPT_EDGE",EDGE,{"disambiguationData":[OSD([sQuery(id+"F47.wireOp",EDGE,"E126"),sQuery(id+"F47.wireOp",EDGE,"E127")])]});
            var Q5;
            Q5=makeQuery(id+"F48.opExtrude","SWEPT_EDGE",EDGE,{"disambiguationData":[OSD([sQuery(id+"F47.wireOp",EDGE,"E126"),sQuery(id+"F47.wireOp",EDGE,"E127")])]});
            var Q6;
            Q6=makeQuery(id+"F49.opExtrude","SWEPT_EDGE",EDGE,{"disambiguationData":[OSD([sQuery(id+"F47.wireOp",EDGE,"E124"),sQuery(id+"F47.wireOp",EDGE,"E127")])]});
            var Q7;
            Q7=makeQuery(id+"F48.opExtrude","SWEPT_EDGE",EDGE,{"disambiguationData":[OSD([sQuery(id+"F47.wireOp",EDGE,"E124"),sQuery(id+"F47.wireOp",EDGE,"E127")])]});
            var Q8;
            Q8=makeQuery(id+"F49.opExtrude","SWEPT_EDGE",EDGE,{"disambiguationData":[OSD([sQuery(id+"F47.wireOp",EDGE,"20FqZ1HW-nhpa-fodr-DXJK-6u80PBLsJZi3"),sQuery(id+"F47.wireOp",EDGE,"E124")])]});
            var Q9;
            Q9=makeQuery(id+"F48.opExtrude","SWEPT_EDGE",EDGE,{"disambiguationData":[OSD([sQuery(id+"F47.wireOp",EDGE,"20FqZ1HW-nhpa-fodr-DXJK-6u80PBLsJZi3"),sQuery(id+"F47.wireOp",EDGE,"E124")])]});
            var Q10;
            Q10=makeQuery(id+"F49.opExtrude","SWEPT_EDGE",EDGE,{"disambiguationData":[OSD([sQuery(id+"F47.wireOp",EDGE,"c1tvB95E-VLiR-0DcJ-Cz1R-gRm9P8e078v8"),sQuery(id+"F47.wireOp",EDGE,"20FqZ1HW-nhpa-fodr-DXJK-6u80PBLsJZi3")])]});
            var Q11;
            Q11=makeQuery(id+"F48.opExtrude","SWEPT_EDGE",EDGE,{"disambiguationData":[OSD([sQuery(id+"F47.wireOp",EDGE,"c1tvB95E-VLiR-0DcJ-Cz1R-gRm9P8e078v8"),sQuery(id+"F47.wireOp",EDGE,"20FqZ1HW-nhpa-fodr-DXJK-6u80PBLsJZi3")])]});
            var Q12;
            Q12=makeQuery(id+"F49.opExtrude","SWEPT_EDGE",EDGE,{"disambiguationData":[OSD([sQuery(id+"F47.wireOp",EDGE,"40H9p0Nx-gS3a-jbsE-J0sd-cglVmnDpoqKR"),sQuery(id+"F47.wireOp",EDGE,"c1tvB95E-VLiR-0DcJ-Cz1R-gRm9P8e078v8")])]});
            var Q13;
            Q13=makeQuery(id+"F48.opExtrude","SWEPT_EDGE",EDGE,{"disambiguationData":[OSD([sQuery(id+"F47.wireOp",EDGE,"40H9p0Nx-gS3a-jbsE-J0sd-cglVmnDpoqKR"),sQuery(id+"F47.wireOp",EDGE,"c1tvB95E-VLiR-0DcJ-Cz1R-gRm9P8e078v8")])]});
            var Q14;
            Q14=makeQuery(id+"F48.opExtrude","SWEPT_EDGE",EDGE,{"disambiguationData":[OSD([sQuery(id+"F47.wireOp",EDGE,"E122"),sQuery(id+"F47.wireOp",EDGE,"40H9p0Nx-gS3a-jbsE-J0sd-cglVmnDpoqKR")])]});
            var Q15;
            Q15=makeQuery(id+"F49.opExtrude","SWEPT_EDGE",EDGE,{"disambiguationData":[OSD([sQuery(id+"F47.wireOp",EDGE,"E122"),sQuery(id+"F47.wireOp",EDGE,"40H9p0Nx-gS3a-jbsE-J0sd-cglVmnDpoqKR")])]});
            var Q16;
            {var subQ0=sQuery(id+"F50.wireOp",EDGE,"E138.bottom");Q16=makeQuery(id+"F51.boolean.opBoolean","COPY",EDGE,{"disambiguationData":[topologyDisambiguationEdgeConnected([makeQuery(id+"F49.opExtrude","SWEPT_FACE",FACE,{"disambiguationData":[OSD([sQuery(id+"F47.wireOp",EDGE,"E122")])]})])],"derivedFrom":makeQuery(id+"F51.opExtrude","CAP_EDGE",EDGE,{"disambiguationData":[OSD([subQ0])],"isStart":true})});}
            var Q17;
            {var subQ0=sQuery(id+"F50.wireOp",EDGE,"E138.bottom");Q17=makeQuery(id+"F51.boolean.opBoolean","COPY",EDGE,{"disambiguationData":[topologyDisambiguationEdgeConnected([makeQuery(id+"F48.opExtrude","SWEPT_FACE",FACE,{"disambiguationData":[OSD([sQuery(id+"F47.wireOp",EDGE,"E122")])]})])],"derivedFrom":makeQuery(id+"F51.opExtrude","CAP_EDGE",EDGE,{"disambiguationData":[OSD([subQ0])],"isStart":true})});}
            var Q18;
            {var subQ0=sQuery(id+"F50.wireOp",EDGE,"E138.top");Q18=makeQuery(id+"F51.boolean.opBoolean","COPY",EDGE,{"disambiguationData":[topologyDisambiguationEdgeConnected([makeQuery(id+"F49.opExtrude","SWEPT_FACE",FACE,{"disambiguationData":[OSD([sQuery(id+"F47.wireOp",EDGE,"E122")])]})])],"derivedFrom":makeQuery(id+"F51.opExtrude","CAP_EDGE",EDGE,{"disambiguationData":[OSD([subQ0])],"isStart":true})});}
            var Q19;
            {var subQ0=sQuery(id+"F50.wireOp",EDGE,"E138.top");Q19=makeQuery(id+"F51.boolean.opBoolean","COPY",EDGE,{"disambiguationData":[topologyDisambiguationEdgeConnected([makeQuery(id+"F48.opExtrude","SWEPT_FACE",FACE,{"disambiguationData":[OSD([sQuery(id+"F47.wireOp",EDGE,"E122")])]})])],"derivedFrom":makeQuery(id+"F51.opExtrude","CAP_EDGE",EDGE,{"disambiguationData":[OSD([subQ0])],"isStart":true})});}
            var Q20;
            Q20=makeQuery(id+"F49.opExtrude","SWEPT_EDGE",EDGE,{"disambiguationData":[OSD([sQuery(id+"F47.wireOp",EDGE,"E122"),sQuery(id+"F47.wireOp",EDGE,"vHFABqv0-Ybvm-PYqP-B5kJ-UVV6UIBHEKYA")])]});
            var Q21;
            Q21=makeQuery(id+"F48.opExtrude","SWEPT_EDGE",EDGE,{"disambiguationData":[OSD([sQuery(id+"F47.wireOp",EDGE,"E122"),sQuery(id+"F47.wireOp",EDGE,"vHFABqv0-Ybvm-PYqP-B5kJ-UVV6UIBHEKYA")])]});
            var Q22;
            Q22=makeQuery(id+"F48.opExtrude","SWEPT_EDGE",EDGE,{"disambiguationData":[OSD([sQuery(id+"F47.wireOp",EDGE,"vHFABqv0-Ybvm-PYqP-B5kJ-UVV6UIBHEKYA"),sQuery(id+"F47.wireOp",EDGE,"80JhjZWx-GQqo-LaVo-pp9a-fqlwG0YZ1vDd")])]});
            var Q23;
            Q23=makeQuery(id+"F49.opExtrude","SWEPT_EDGE",EDGE,{"disambiguationData":[OSD([sQuery(id+"F47.wireOp",EDGE,"vHFABqv0-Ybvm-PYqP-B5kJ-UVV6UIBHEKYA"),sQuery(id+"F47.wireOp",EDGE,"80JhjZWx-GQqo-LaVo-pp9a-fqlwG0YZ1vDd")])]});
            var Q24;
            Q24=makeQuery(id+"F48.opExtrude","SWEPT_EDGE",EDGE,{"disambiguationData":[OSD([sQuery(id+"F47.wireOp",EDGE,"80JhjZWx-GQqo-LaVo-pp9a-fqlwG0YZ1vDd"),sQuery(id+"F47.wireOp",EDGE,"qFPor4tA-krSn-UBEH-swcX-wpI3ccUzTAWm")])]});
            var Q25;
            Q25=makeQuery(id+"F49.opExtrude","SWEPT_EDGE",EDGE,{"disambiguationData":[OSD([sQuery(id+"F47.wireOp",EDGE,"80JhjZWx-GQqo-LaVo-pp9a-fqlwG0YZ1vDd"),sQuery(id+"F47.wireOp",EDGE,"qFPor4tA-krSn-UBEH-swcX-wpI3ccUzTAWm")])]});
            var Q26;
            Q26=makeQuery(id+"F49.opExtrude","SWEPT_EDGE",EDGE,{"disambiguationData":[OSD([sQuery(id+"F47.wireOp",EDGE,"qFPor4tA-krSn-UBEH-swcX-wpI3ccUzTAWm"),sQuery(id+"F47.wireOp",EDGE,"E123")])]});
            var Q27;
            Q27=makeQuery(id+"F48.opExtrude","SWEPT_EDGE",EDGE,{"disambiguationData":[OSD([sQuery(id+"F47.wireOp",EDGE,"qFPor4tA-krSn-UBEH-swcX-wpI3ccUzTAWm"),sQuery(id+"F47.wireOp",EDGE,"E123")])]});
            var Q28;
            Q28=makeQuery(id+"F51.boolean.opBoolean","INTERSECT",EDGE,{"derivedFrom":[makeQuery(id+"F49.opExtrude","SWEPT_FACE",FACE,{"disambiguationData":[OSD([sQuery(id+"F47.wireOp",EDGE,"E126")])]}),makeQuery(id+"F51.opExtrude","SWEPT_FACE",FACE,{"disambiguationData":[OSD([sQuery(id+"F50.wireOp",EDGE,"E138.top")])]})]});
            var Q29;
            Q29=makeQuery(id+"F51.boolean.opBoolean","INTERSECT",EDGE,{"derivedFrom":[makeQuery(id+"F48.opExtrude","SWEPT_FACE",FACE,{"disambiguationData":[OSD([sQuery(id+"F47.wireOp",EDGE,"E126")])]}),makeQuery(id+"F51.opExtrude","SWEPT_FACE",FACE,{"disambiguationData":[OSD([sQuery(id+"F50.wireOp",EDGE,"E138.top")])]})]});
            var Q30;
            Q30=makeQuery(id+"F51.boolean.opBoolean","INTERSECT",EDGE,{"derivedFrom":[makeQuery(id+"F48.opExtrude","SWEPT_FACE",FACE,{"disambiguationData":[OSD([sQuery(id+"F47.wireOp",EDGE,"E126")])]}),makeQuery(id+"F51.opExtrude","SWEPT_FACE",FACE,{"disambiguationData":[OSD([sQuery(id+"F50.wireOp",EDGE,"E138.bottom")])]})]});
            var Q31;
            Q31=makeQuery(id+"F51.boolean.opBoolean","INTERSECT",EDGE,{"derivedFrom":[makeQuery(id+"F49.opExtrude","SWEPT_FACE",FACE,{"disambiguationData":[OSD([sQuery(id+"F47.wireOp",EDGE,"E126")])]}),makeQuery(id+"F51.opExtrude","SWEPT_FACE",FACE,{"disambiguationData":[OSD([sQuery(id+"F50.wireOp",EDGE,"E138.bottom")])]})]});
            var Q32;
            Q32=makeQuery(id+"F48.opExtrude","SWEPT_EDGE",EDGE,{"disambiguationData":[OSD([sQuery(id+"F47.wireOp",EDGE,"E128"),sQuery(id+"F47.wireOp",EDGE,"E131")])]});
            var Q33;
            Q33=makeQuery(id+"F49.opExtrude","SWEPT_EDGE",EDGE,{"disambiguationData":[OSD([sQuery(id+"F47.wireOp",EDGE,"E128"),sQuery(id+"F47.wireOp",EDGE,"E131")])]});
            var Q34;
            Q34=makeQuery(id+"F49.opExtrude","SWEPT_EDGE",EDGE,{"disambiguationData":[OSD([sQuery(id+"F47.wireOp",EDGE,"E129"),sQuery(id+"F47.wireOp",EDGE,"E130")])]});
            var Q35;
            Q35=makeQuery(id+"F48.opExtrude","SWEPT_EDGE",EDGE,{"disambiguationData":[OSD([sQuery(id+"F47.wireOp",EDGE,"E129"),sQuery(id+"F47.wireOp",EDGE,"E130")])]});
            var Q36;
            Q36=makeQuery(id+"F48.opExtrude","SWEPT_EDGE",EDGE,{"disambiguationData":[OSD([sQuery(id+"F47.wireOp",EDGE,"E133"),sQuery(id+"F47.wireOp",EDGE,"E134")])]});
            var Q37;
            Q37=makeQuery(id+"F49.opExtrude","SWEPT_EDGE",EDGE,{"disambiguationData":[OSD([sQuery(id+"F47.wireOp",EDGE,"E133"),sQuery(id+"F47.wireOp",EDGE,"E134")])]});
            var Q38;
            Q38=makeQuery(id+"F49.opExtrude","SWEPT_EDGE",EDGE,{"disambiguationData":[OSD([sQuery(id+"F47.wireOp",EDGE,"E132"),sQuery(id+"F47.wireOp",EDGE,"E133")])]});
            var Q39;
            Q39=makeQuery(id+"F48.opExtrude","SWEPT_EDGE",EDGE,{"disambiguationData":[OSD([sQuery(id+"F47.wireOp",EDGE,"E132"),sQuery(id+"F47.wireOp",EDGE,"E133")])]});
            var Q40;
            Q40=makeQuery(id+"F49.opExtrude","SWEPT_EDGE",EDGE,{"disambiguationData":[OSD([sQuery(id+"F47.wireOp",EDGE,"E135"),sQuery(id+"F47.wireOp",EDGE,"E136")])]});
            var Q41;
            Q41=makeQuery(id+"F48.opExtrude","SWEPT_EDGE",EDGE,{"disambiguationData":[OSD([sQuery(id+"F47.wireOp",EDGE,"E135"),sQuery(id+"F47.wireOp",EDGE,"E136")])]});
            var Q42;
            Q42=makeQuery(id+"F49.opExtrude","SWEPT_EDGE",EDGE,{"disambiguationData":[OSD([sQuery(id+"F47.wireOp",EDGE,"E136"),sQuery(id+"F47.wireOp",EDGE,"E137")])]});
            var Q43;
            Q43=makeQuery(id+"F48.opExtrude","SWEPT_EDGE",EDGE,{"disambiguationData":[OSD([sQuery(id+"F47.wireOp",EDGE,"E136"),sQuery(id+"F47.wireOp",EDGE,"E137")])]});
            fillet(context, id + "F79", {"entities" : qUnion([Q0, Q1, Q2, Q3, Q4, Q5, Q6, Q7, Q8, Q9, Q10, Q11, Q12, Q13, Q14, Q15, Q16, Q17, Q18, Q19, Q20, Q21, Q22, Q23, Q24, Q25, Q26, Q27, Q28, Q29, Q30, Q31, Q32, Q33, Q34, Q35, Q36, Q37, Q38, Q39, Q40, Q41, Q42, Q43]), "radius" : getVariable(context, 'FilletRadius'), "tangentPropagation" : true, "allowEdgeOverflow" : false});
        }
        {
            var Q0;
            Q0=makeQuery(id+"F55.boolean.opBoolean","MERGE",FACE,{"derivedFrom":[makeQuery(id+"F49.opExtrude","SWEPT_FACE",FACE,{"disambiguationData":[OSD([sQuery(id+"F47.wireOp",EDGE,"E125")])]}),makeQuery(id+"F55.opExtrude","CAP_FACE",FACE,{"disambiguationData":[OSD([sQuery(id+"F54.wireOp",EDGE,"E144"),sQuery(id+"F54.wireOp",EDGE,"E145"),sQuery(id+"F54.wireOp",EDGE,"E146"),sQuery(id+"F54.wireOp",EDGE,"E147"),sQuery(id+"F54.wireOp",EDGE,"E148")])],"isStart":true})]});
            var sketch = newSketch(context, id + "F80", { "sketchPlane" : qUnion([Q0])});
            skCircle(sketch, "E228", {"center": v(38.04, -13) * mm, "radius": 12.5 * mm});
            skSolve(sketch);
        }
        {
            var Q0;
            Q0 = qSketchRegion(id + "F80", true);
            extrude(context, id + "F81", {"entities" : qUnion([Q0]), "operationType" : NewBodyOperationType.REMOVE, "depth" : 25 * mm, "offsetDistance" : 25 * mm});
        }
        {
            var Q0;
            Q0=makeQuery(id+"F49.opExtrude","CAP_FACE",FACE,{"disambiguationData":[OSD([sQuery(id+"F47.wireOp",EDGE,"E122"),sQuery(id+"F47.wireOp",EDGE,"vHFABqv0-Ybvm-PYqP-B5kJ-UVV6UIBHEKYA"),sQuery(id+"F47.wireOp",EDGE,"80JhjZWx-GQqo-LaVo-pp9a-fqlwG0YZ1vDd"),sQuery(id+"F47.wireOp",EDGE,"qFPor4tA-krSn-UBEH-swcX-wpI3ccUzTAWm"),sQuery(id+"F47.wireOp",EDGE,"40H9p0Nx-gS3a-jbsE-J0sd-cglVmnDpoqKR"),sQuery(id+"F47.wireOp",EDGE,"c1tvB95E-VLiR-0DcJ-Cz1R-gRm9P8e078v8"),sQuery(id+"F47.wireOp",EDGE,"20FqZ1HW-nhpa-fodr-DXJK-6u80PBLsJZi3"),sQuery(id+"F47.wireOp",EDGE,"E123"),sQuery(id+"F47.wireOp",EDGE,"E124"),sQuery(id+"F47.wireOp",EDGE,"E125"),sQuery(id+"F47.wireOp",EDGE,"E126"),sQuery(id+"F47.wireOp",EDGE,"E127")])],"isStart":false});
            var sketch = newSketch(context, id + "F82", { "sketchPlane" : qUnion([Q0])});
            skCircle(sketch, "E229", {"center": v(21.54, 15.33) * mm, "radius": 2.85 * mm});
            skCircle(sketch, "E230", {"center": v(21.54, 85.33) * mm, "radius": 2.85 * mm});
            skCircle(sketch, "E231", {"center": v(66.54, 85.33) * mm, "radius": 2.85 * mm});
            skCircle(sketch, "E232", {"center": v(66.54, 15.33) * mm, "radius": 2.85 * mm});
            skSolve(sketch);
        }
        {
            var Q0;
            Q0 = qSketchRegion(id + "F82", true);
            extrude(context, id + "F83", {"entities" : qUnion([Q0]), "operationType" : NewBodyOperationType.REMOVE, "oppositeDirection" : true, "depth" : getVariable(context, 'M3HeadRecessDepth'), "offsetDistance" : 25 * mm});
        }
        {
            var Q0;
            {var subQ0=sQuery(id+"F52.wireOp",EDGE,"E139");Q0=makeQuery(id+"F53.boolean.opBoolean","COPY",FACE,{"disambiguationData":[TD([makeQuery(id+"F48.opExtrude","CAP_FACE",FACE,{"disambiguationData":[OSD([sQuery(id+"F47.wireOp",EDGE,"E122"),sQuery(id+"F47.wireOp",EDGE,"E123"),sQuery(id+"F47.wireOp",EDGE,"E124"),sQuery(id+"F47.wireOp",EDGE,"E125"),sQuery(id+"F47.wireOp",EDGE,"E126"),sQuery(id+"F47.wireOp",EDGE,"E127"),sQuery(id+"F47.wireOp",EDGE,"E128"),sQuery(id+"F47.wireOp",EDGE,"E129"),sQuery(id+"F47.wireOp",EDGE,"E130"),sQuery(id+"F47.wireOp",EDGE,"E131"),sQuery(id+"F47.wireOp",EDGE,"E132"),sQuery(id+"F47.wireOp",EDGE,"E133"),sQuery(id+"F47.wireOp",EDGE,"E134"),sQuery(id+"F47.wireOp",EDGE,"E135"),sQuery(id+"F47.wireOp",EDGE,"E136"),sQuery(id+"F47.wireOp",EDGE,"E137")])],"isStart":true})])],"derivedFrom":makeQuery(id+"F53.opExtrude","CAP_FACE",FACE,{"disambiguationData":[OSD([subQ0])],"isStart":false})});}
            var sketch = newSketch(context, id + "F84", { "sketchPlane" : qUnion([Q0])});
            skCircle(sketch, "E233", {"center": v(0, 72.83) * mm, "radius": 2.7 * mm});
            skCircle(sketch, "E234", {"center": v(0, 27.83) * mm, "radius": 2.7 * mm});
            skSolve(sketch);
        }
        {
            var Q0;
            {var subQ0=sQuery(id+"F28.wireOp",EDGE,"E67");Q0=makeQuery(id+"F29.boolean.opBoolean","MERGE",FACE,{"derivedFrom":[makeQuery(id+"F10.opExtrude","SWEPT_FACE",FACE,{"disambiguationData":[OSD([sQuery(id+"F8.wireOp",EDGE,"E0")])]}),makeQuery(id+"F29.opExtrude","CAP_FACE",FACE,{"disambiguationData":[OSD([subQ0,sQuery(id+"F28.wireOp",EDGE,"E69"),sQuery(id+"F28.wireOp",EDGE,"E72"),sQuery(id+"F28.wireOp",EDGE,"E73")])],"isStart":true}),makeQuery(id+"F29.opExtrude","CAP_FACE",FACE,{"disambiguationData":[OSD([subQ0,sQuery(id+"F28.wireOp",EDGE,"E68"),sQuery(id+"F28.wireOp",EDGE,"E70"),sQuery(id+"F28.wireOp",EDGE,"E71")])],"isStart":true})]});}
            var sketch = newSketch(context, id + "F85", { "sketchPlane" : qUnion([Q0])});
            skArc(sketch, "E235", {"start": v(-44.8, 13) * mm, "mid": v(-52.4, 20.6) * mm, "end": v(-60, 13) * mm});
            skLineSegment(sketch, "E236", {"start": v(-60, 13) * mm, "end": v(-64.76, 13) * mm});
            skLineSegment(sketch, "E237", {"start": v(-44.8, 13) * mm, "end": v(-40.06, 13) * mm});
            skLineSegment(sketch, "E238", {"start": v(-64.76, 13) * mm, "end": v(-64.76, 23) * mm});
            skLineSegment(sketch, "E239", {"start": v(-40.06, 13) * mm, "end": v(-40.06, 23) * mm});
            skLineSegment(sketch, "E240", {"start": v(-64.76, 23) * mm, "end": v(-40.06, 23) * mm});
            skSolve(sketch);
        }
        {
            var Q0;
            Q0 = qSketchRegion(id + "F85", true);
            extrude(context, id + "F86", {"entities" : qUnion([Q0]), "oppositeDirection" : true, "depth" : 5 * mm + getVariable(context, 'Tolerance') / 2, "offsetDistance" : 25 * mm});
        }
        {
            var Q0;
            Q0=makeQuery(id+"F86.opExtrude","CAP_FACE",FACE,{"disambiguationData":[OSD([sQuery(id+"F85.wireOp",EDGE,"E235"),sQuery(id+"F85.wireOp",EDGE,"E236"),sQuery(id+"F85.wireOp",EDGE,"E237"),sQuery(id+"F85.wireOp",EDGE,"E238"),sQuery(id+"F85.wireOp",EDGE,"E239"),sQuery(id+"F85.wireOp",EDGE,"E240")])],"isStart":false});
            var sketch = newSketch(context, id + "F87", { "sketchPlane" : qUnion([Q0])});
            skArc(sketch, "E241", {"start": v(-45.16, -13) * mm, "mid": v(-52.4, -20.25) * mm, "end": v(-59.66, -13) * mm});
            skLineSegment(sketch, "E242", {"start": v(-59.66, -13) * mm, "end": v(-64.76, -13) * mm});
            skLineSegment(sketch, "E243", {"start": v(-64.76, -13) * mm, "end": v(-64.76, -23) * mm});
            skLineSegment(sketch, "E244", {"start": v(-64.76, -23) * mm, "end": v(-40.06, -23) * mm});
            skLineSegment(sketch, "E245", {"start": v(-40.06, -23) * mm, "end": v(-40.06, -13) * mm});
            skLineSegment(sketch, "E246", {"start": v(-40.06, -13) * mm, "end": v(-45.16, -13) * mm});
            skSolve(sketch);
        }
        {
            var Q0;
            Q0 = qSketchRegion(id + "F87", true);
            extrude(context, id + "F88", {"entities" : qUnion([Q0]), "operationType" : NewBodyOperationType.ADD, "depth" : 1.1 * mm - getVariable(context, 'Tolerance'), "offsetDistance" : 25 * mm});
        }
        {
            var Q0;
            Q0=makeQuery(id+"F88.opExtrude","CAP_FACE",FACE,{"disambiguationData":[OSD([sQuery(id+"F87.wireOp",EDGE,"E241"),sQuery(id+"F87.wireOp",EDGE,"E242"),sQuery(id+"F87.wireOp",EDGE,"E243"),sQuery(id+"F87.wireOp",EDGE,"E244"),sQuery(id+"F87.wireOp",EDGE,"E245"),sQuery(id+"F87.wireOp",EDGE,"E246")])],"isStart":false});
            var sketch = newSketch(context, id + "F89", { "sketchPlane" : qUnion([Q0])});
            skArc(sketch, "E247", {"start": v(-44.8, -13) * mm, "mid": v(-52.4, -20.6) * mm, "end": v(-60, -13) * mm});
            skLineSegment(sketch, "E248", {"start": v(-60, -13) * mm, "end": v(-64.76, -13) * mm});
            skLineSegment(sketch, "E249", {"start": v(-64.76, -13) * mm, "end": v(-64.76, -23) * mm});
            skLineSegment(sketch, "E250", {"start": v(-64.76, -23) * mm, "end": v(-40.06, -23) * mm});
            skLineSegment(sketch, "E251", {"start": v(-40.06, -23) * mm, "end": v(-40.06, -13) * mm});
            skLineSegment(sketch, "E252", {"start": v(-40.06, -13) * mm, "end": v(-44.8, -13) * mm});
            skSolve(sketch);
        }
        {
            var Q0;
            Q0 = qSketchRegion(id + "F89", true);
            extrude(context, id + "F90", {"entities" : qUnion([Q0]), "operationType" : NewBodyOperationType.ADD, "depth" : 32.8 * mm + getVariable(context, 'Tolerance'), "offsetDistance" : 25 * mm});
        }
        {
            var Q0;
            Q0=makeQuery(id+"F90.opExtrude","CAP_FACE",FACE,{"disambiguationData":[OSD([sQuery(id+"F89.wireOp",EDGE,"E247"),sQuery(id+"F89.wireOp",EDGE,"E248"),sQuery(id+"F89.wireOp",EDGE,"E249"),sQuery(id+"F89.wireOp",EDGE,"E250"),sQuery(id+"F89.wireOp",EDGE,"E251"),sQuery(id+"F89.wireOp",EDGE,"E252")])],"isStart":false});
            var sketch = newSketch(context, id + "F91", { "sketchPlane" : qUnion([Q0])});
            skArc(sketch, "E253", {"start": v(-45.16, -13) * mm, "mid": v(-52.4, -20.25) * mm, "end": v(-59.66, -13) * mm});
            skLineSegment(sketch, "E254", {"start": v(-59.66, -13) * mm, "end": v(-64.76, -13) * mm});
            skLineSegment(sketch, "E255", {"start": v(-64.76, -13) * mm, "end": v(-64.76, -23) * mm});
            skLineSegment(sketch, "E256", {"start": v(-64.76, -23) * mm, "end": v(-40.06, -23) * mm});
            skLineSegment(sketch, "E257", {"start": v(-40.06, -23) * mm, "end": v(-40.06, -13) * mm});
            skLineSegment(sketch, "E258", {"start": v(-40.06, -13) * mm, "end": v(-45.16, -13) * mm});
            skSolve(sketch);
        }
        {
            var Q0;
            Q0 = qSketchRegion(id + "F91", true);
            extrude(context, id + "F92", {"entities" : qUnion([Q0]), "operationType" : NewBodyOperationType.ADD, "depth" : 1.1 * mm - getVariable(context, 'Tolerance'), "offsetDistance" : 25 * mm});
        }
        {
            var Q0;
            Q0=makeQuery(id+"F92.opExtrude","CAP_FACE",FACE,{"disambiguationData":[OSD([sQuery(id+"F91.wireOp",EDGE,"E253"),sQuery(id+"F91.wireOp",EDGE,"E254"),sQuery(id+"F91.wireOp",EDGE,"E255"),sQuery(id+"F91.wireOp",EDGE,"E256"),sQuery(id+"F91.wireOp",EDGE,"E257"),sQuery(id+"F91.wireOp",EDGE,"E258")])],"isStart":false});
            var sketch = newSketch(context, id + "F93", { "sketchPlane" : qUnion([Q0])});
            skArc(sketch, "E259", {"start": v(-44.8, -13) * mm, "mid": v(-52.4, -20.6) * mm, "end": v(-60, -13) * mm});
            skLineSegment(sketch, "E260", {"start": v(-60, -13) * mm, "end": v(-64.76, -13) * mm});
            skLineSegment(sketch, "E261", {"start": v(-64.76, -13) * mm, "end": v(-64.76, -23) * mm});
            skLineSegment(sketch, "E262", {"start": v(-64.76, -23) * mm, "end": v(-40.06, -23) * mm});
            skLineSegment(sketch, "E263", {"start": v(-40.06, -23) * mm, "end": v(-40.06, -13) * mm});
            skLineSegment(sketch, "E264", {"start": v(-40.06, -13) * mm, "end": v(-44.8, -13) * mm});
            skSolve(sketch);
        }
        {
            var Q0;
            Q0 = qSketchRegion(id + "F93", true);
            extrude(context, id + "F94", {"entities" : qUnion([Q0]), "operationType" : NewBodyOperationType.ADD, "depth" : 5 * mm + getVariable(context, 'Tolerance') / 2, "offsetDistance" : 25 * mm});
        }
        {
            var Q0;
            Q0 = qSketchRegion(id + "F38", true);
            extrude(context, id + "F95", {"entities" : qUnion([Q0]), "operationType" : NewBodyOperationType.REMOVE, "depth" : 25 * mm, "offsetDistance" : 25 * mm});
        }
        {
            var Q0;
            Q0=makeQuery(id+"F49.opExtrude","SWEPT_FACE",FACE,{"disambiguationData":[OSD([sQuery(id+"F47.wireOp",EDGE,"E126")])]});
            var sketch = newSketch(context, id + "F96", { "sketchPlane" : qUnion([Q0])});
            skLineSegment(sketch, "E265.bottom", {"start": v(7, 20.33) * mm, "end": v(-7, 20.33) * mm});
            skLineSegment(sketch, "E265.top", {"start": v(7, 80.33) * mm, "end": v(-7, 80.33) * mm});
            skLineSegment(sketch, "E265.left", {"start": v(7, 20.33) * mm, "end": v(7, 80.33) * mm});
            skLineSegment(sketch, "E265.right", {"start": v(-7, 20.33) * mm, "end": v(-7, 80.33) * mm});
            skPoint(sketch, "E266", {"position": v(0, 20.33) * mm});
            skPoint(sketch, "E267", {"position": v(7, 50.33) * mm});
            skLineSegment(sketch, "E268", {"start": v(-4, 42.83) * mm, "end": v(-4, 50.33) * mm});
            skPoint(sketch, "E269", {"position": v(0, 72.83) * mm});
            skPoint(sketch, "E270", {"position": v(0, 27.83) * mm});
            skCircle(sketch, "E271", {"center": v(0, 72.83) * mm, "radius": 2.7 * mm});
            skCircle(sketch, "E272", {"center": v(0, 27.83) * mm, "radius": 2.7 * mm});
            skPoint(sketch, "E273", {"position": v(-7, 50.33) * mm});
            skLineSegment(sketch, "E274", {"start": v(-4.75, 50.33) * mm, "end": v(-4.75, 60.33) * mm});
            skLineSegment(sketch, "E275", {"start": v(-4.75, 60.33) * mm, "end": v(4.75, 60.33) * mm});
            skLineSegment(sketch, "E276", {"start": v(4.75, 60.33) * mm, "end": v(4.75, 40.33) * mm});
            skLineSegment(sketch, "E277", {"start": v(4.75, 40.33) * mm, "end": v(-4.75, 40.33) * mm});
            skLineSegment(sketch, "E278", {"start": v(-4.75, 50.33) * mm, "end": v(-4.75, 40.33) * mm});
            skLineSegment(sketch, "E279", {"start": v(-7, 60.33) * mm, "end": v(4.75, 60.33) * mm});
            skLineSegment(sketch, "E280", {"start": v(7, 60.33) * mm, "end": v(-4.75, 60.33) * mm});
            skSolve(sketch);
        }
        {
            var Q0;
            Q0 = qSketchRegion(id + "F96", true);
            extrude(context, id + "F97", {"entities" : qUnion([Q0]), "depth" : 20 * mm, "offsetDistance" : 25 * mm});
        }
        {
            var Q0;
            Q0=makeQuery(id+"F97.opExtrude","CAP_EDGE",EDGE,{"disambiguationData":[OSD([sQuery(id+"F96.wireOp",EDGE,"E275")])],"isStart":true});
            var Q1;
            Q1=makeQuery(id+"F97.opExtrude","CAP_EDGE",EDGE,{"disambiguationData":[OSD([sQuery(id+"F96.wireOp",EDGE,"E277")])],"isStart":true});
            var Q2;
            Q2=makeQuery(id+"F97.opExtrude","CAP_EDGE",EDGE,{"disambiguationData":[OSD([sQuery(id+"F96.wireOp",EDGE,"E265.top")])],"isStart":true});
            var Q3;
            Q3=makeQuery(id+"F97.opExtrude","CAP_EDGE",EDGE,{"disambiguationData":[OSD([sQuery(id+"F96.wireOp",EDGE,"E265.top")])],"isStart":false});
            var Q4;
            Q4=makeQuery(id+"F97.opExtrude","CAP_EDGE",EDGE,{"disambiguationData":[OSD([sQuery(id+"F96.wireOp",EDGE,"E265.bottom")])],"isStart":true});
            var Q5;
            Q5=makeQuery(id+"F97.opExtrude","CAP_EDGE",EDGE,{"disambiguationData":[OSD([sQuery(id+"F96.wireOp",EDGE,"E265.bottom")])],"isStart":false});
            var Q6;
            Q6=makeQuery(id+"F97.opExtrude","CAP_EDGE",EDGE,{"disambiguationData":[OSD([sQuery(id+"F96.wireOp",EDGE,"E275")])],"isStart":false});
            var Q7;
            Q7=makeQuery(id+"F97.opExtrude","CAP_EDGE",EDGE,{"disambiguationData":[OSD([sQuery(id+"F96.wireOp",EDGE,"E277")])],"isStart":false});
            fillet(context, id + "F98", {"entities" : qUnion([Q0, Q1, Q2, Q3, Q4, Q5, Q6, Q7]), "radius" : getVariable(context, 'FilletRadius'), "tangentPropagation" : true, "allowEdgeOverflow" : false});
        }
        {
            var Q0;
            Q0=makeQuery(id+"F97.opExtrude","SWEPT_FACE",FACE,{"disambiguationData":[OSD([sQuery(id+"F96.wireOp",EDGE,"E265.left")])]});
            var sketch = newSketch(context, id + "F99", { "sketchPlane" : qUnion([Q0])});
            skCircle(sketch, "E281", {"center": v(-81.54, 50.33) * mm, "radius": 1.7 * mm});
            skPoint(sketch, "E281.centerSnap0", {"position": v(-91.54, 50.33) * mm});
            skPoint(sketch, "E281.centerSnap1", {"position": v(-81.54, 20.33) * mm});
            skSolve(sketch);
        }
        {
            var Q0;
            Q0 = qSketchRegion(id + "F99", true);
            extrude(context, id + "F100", {"entities" : qUnion([Q0]), "operationType" : NewBodyOperationType.REMOVE, "oppositeDirection" : true, "depth" : 25 * mm, "offsetDistance" : 25 * mm});
        }
        {
            var Q0;
            Q0=makeQuery(id+"F97.opExtrude","CAP_FACE",FACE,{"disambiguationData":[OSD([sQuery(id+"F96.wireOp",EDGE,"E265.bottom"),sQuery(id+"F96.wireOp",EDGE,"E265.top"),sQuery(id+"F96.wireOp",EDGE,"E265.left"),sQuery(id+"F96.wireOp",EDGE,"E265.right"),sQuery(id+"F96.wireOp",EDGE,"ybWAz7j5-wVdk-dy6P-jYDY-Ey7IVQyTHfUg"),sQuery(id+"F96.wireOp",EDGE,"pjWf2qMF-NiQv-hnjn-Qs4j-6vSIXw0rLLed"),sQuery(id+"F96.wireOp",EDGE,"MTkrlTaa-yLgv-pJMc-0rbu-33LRPnyCgddg"),sQuery(id+"F96.wireOp",EDGE,"eWNKoOYc-D1fA-v94E-mFUH-Giex7sB2EK62"),sQuery(id+"F96.wireOp",EDGE,"E268"),sQuery(id+"F96.wireOp",EDGE,"E271"),sQuery(id+"F96.wireOp",EDGE,"E272")])],"isStart":true});
            var sketch = newSketch(context, id + "F101", { "sketchPlane" : qUnion([Q0])});
            skCircle(sketch, "E282.cCircle", {"center": v(0, 72.83) * mm, "radius": 4.05 * mm, "construction": true});
            skLineSegment(sketch, "E282.0", {"start": v(-2.34, 76.88) * mm, "end": v(2.34, 76.88) * mm});
            skLineSegment(sketch, "E282.1", {"start": v(2.34, 76.88) * mm, "end": v(4.68, 72.83) * mm});
            skLineSegment(sketch, "E282.2", {"start": v(4.68, 72.83) * mm, "end": v(2.34, 68.78) * mm});
            skLineSegment(sketch, "E282.3", {"start": v(2.34, 68.78) * mm, "end": v(-2.34, 68.78) * mm});
            skLineSegment(sketch, "E282.4", {"start": v(-2.34, 68.78) * mm, "end": v(-4.68, 72.83) * mm});
            skLineSegment(sketch, "E282.5", {"start": v(-4.68, 72.83) * mm, "end": v(-2.34, 76.88) * mm});
            skPoint(sketch, "E282.0.midPoint", {"position": v(0, 76.88) * mm});
            skCircle(sketch, "E283.cCircle", {"center": v(0, 27.83) * mm, "radius": 4.05 * mm, "construction": true});
            skLineSegment(sketch, "E283.0", {"start": v(-2.34, 31.88) * mm, "end": v(2.34, 31.88) * mm});
            skLineSegment(sketch, "E283.1", {"start": v(2.34, 31.88) * mm, "end": v(4.68, 27.83) * mm});
            skLineSegment(sketch, "E283.2", {"start": v(4.68, 27.83) * mm, "end": v(2.34, 23.78) * mm});
            skLineSegment(sketch, "E283.3", {"start": v(2.34, 23.78) * mm, "end": v(-2.34, 23.78) * mm});
            skLineSegment(sketch, "E283.4", {"start": v(-2.34, 23.78) * mm, "end": v(-4.68, 27.83) * mm});
            skLineSegment(sketch, "E283.5", {"start": v(-4.68, 27.83) * mm, "end": v(-2.34, 31.88) * mm});
            skPoint(sketch, "E283.0.midPoint", {"position": v(0, 31.88) * mm});
            skSolve(sketch);
        }
        {
            var Q0;
            Q0 = qSketchRegion(id + "F101", true);
            extrude(context, id + "F102", {"entities" : qUnion([Q0]), "operationType" : NewBodyOperationType.REMOVE, "oppositeDirection" : true, "depth" : getVariable(context, 'M5HexNutDepth'), "offsetDistance" : 25 * mm});
        }
        {
            var Q0;
            Q0=makeQuery(id+"F97.opExtrude","CAP_FACE",FACE,{"disambiguationData":[OSD([sQuery(id+"F96.wireOp",EDGE,"E265.bottom"),sQuery(id+"F96.wireOp",EDGE,"E265.top"),sQuery(id+"F96.wireOp",EDGE,"E265.left"),sQuery(id+"F96.wireOp",EDGE,"E265.right"),sQuery(id+"F96.wireOp",EDGE,"ybWAz7j5-wVdk-dy6P-jYDY-Ey7IVQyTHfUg"),sQuery(id+"F96.wireOp",EDGE,"pjWf2qMF-NiQv-hnjn-Qs4j-6vSIXw0rLLed"),sQuery(id+"F96.wireOp",EDGE,"MTkrlTaa-yLgv-pJMc-0rbu-33LRPnyCgddg"),sQuery(id+"F96.wireOp",EDGE,"eWNKoOYc-D1fA-v94E-mFUH-Giex7sB2EK62"),sQuery(id+"F96.wireOp",EDGE,"E268"),sQuery(id+"F96.wireOp",EDGE,"E271"),sQuery(id+"F96.wireOp",EDGE,"E272")])],"isStart":false});
            var sketch = newSketch(context, id + "F103", { "sketchPlane" : qUnion([Q0])});
            skCircle(sketch, "E284", {"center": v(0, 72.83) * mm, "radius": 4.35 * mm});
            skCircle(sketch, "E285", {"center": v(0, 27.83) * mm, "radius": 4.35 * mm});
            skSolve(sketch);
        }
        {
            var Q0;
            Q0 = qSketchRegion(id + "F103", true);
            extrude(context, id + "F104", {"entities" : qUnion([Q0]), "operationType" : NewBodyOperationType.REMOVE, "oppositeDirection" : true, "depth" : getVariable(context, 'M5HeadRecessDepth'), "offsetDistance" : 25 * mm});
        }
        {
            var Q0;
            Q0=makeQuery(id+"F94.boolean.opBoolean","MERGE",FACE,{"derivedFrom":[makeQuery(id+"F92.boolean.opBoolean","MERGE",FACE,{"derivedFrom":[makeQuery(id+"F90.boolean.opBoolean","MERGE",FACE,{"derivedFrom":[makeQuery(id+"F88.boolean.opBoolean","MERGE",FACE,{"derivedFrom":[makeQuery(id+"F86.opExtrude","SWEPT_FACE",FACE,{"disambiguationData":[OSD([sQuery(id+"F85.wireOp",EDGE,"E240")])]}),makeQuery(id+"F88.opExtrude","SWEPT_FACE",FACE,{"disambiguationData":[OSD([sQuery(id+"F87.wireOp",EDGE,"E244")])]})]}),makeQuery(id+"F90.opExtrude","SWEPT_FACE",FACE,{"disambiguationData":[OSD([sQuery(id+"F89.wireOp",EDGE,"E250")])]})]}),makeQuery(id+"F92.opExtrude","SWEPT_FACE",FACE,{"disambiguationData":[OSD([sQuery(id+"F91.wireOp",EDGE,"E256")])]})]}),makeQuery(id+"F94.opExtrude","SWEPT_FACE",FACE,{"disambiguationData":[OSD([sQuery(id+"F93.wireOp",EDGE,"E262")])]})]});
            var sketch = newSketch(context, id + "F105", { "sketchPlane" : qUnion([Q0])});
            skLineSegment(sketch, "E286.bottom", {"start": v(-64.76, 65) * mm, "end": v(-40.06, 65) * mm});
            skLineSegment(sketch, "E286.top", {"start": v(-64.76, 20) * mm, "end": v(-40.06, 20) * mm});
            skLineSegment(sketch, "E286.left", {"start": v(-64.76, 65) * mm, "end": v(-64.76, 20) * mm});
            skLineSegment(sketch, "E286.right", {"start": v(-40.06, 65) * mm, "end": v(-40.06, 20) * mm});
            skSolve(sketch);
        }
        {
            var Q0;
            Q0 = qSketchRegion(id + "F105", true);
            extrude(context, id + "F106", {"entities" : qUnion([Q0]), "depth" : 3 * mm, "offsetDistance" : 25 * mm});
        }
        {
            var Q0;
            Q0=makeQuery(id+"F106.opExtrude","SWEPT_FACE",FACE,{"disambiguationData":[OSD([sQuery(id+"F105.wireOp",EDGE,"E286.top")])]});
            var sketch = newSketch(context, id + "F107", { "sketchPlane" : qUnion([Q0])});
            skLineSegment(sketch, "E287.bottom", {"start": v(-64.76, 26) * mm, "end": v(-39.96, 26) * mm});
            skLineSegment(sketch, "E287.top", {"start": v(-64.76, 45) * mm, "end": v(-39.96, 45) * mm});
            skLineSegment(sketch, "E287.left", {"start": v(-64.76, 26) * mm, "end": v(-64.76, 45) * mm});
            skLineSegment(sketch, "E287.right", {"start": v(-39.96, 26) * mm, "end": v(-39.96, 45) * mm});
            skSolve(sketch);
        }
        {
            var Q0;
            Q0 = qSketchRegion(id + "F107", true);
            extrude(context, id + "F108", {"entities" : qUnion([Q0]), "operationType" : NewBodyOperationType.ADD, "oppositeDirection" : true, "depth" : 8 * mm, "offsetDistance" : 25 * mm});
        }
        {
            var Q0;
            Q0=makeQuery(id+"F108.opExtrude","CAP_FACE",FACE,{"disambiguationData":[OSD([sQuery(id+"F107.wireOp",EDGE,"E287.bottom"),sQuery(id+"F107.wireOp",EDGE,"E287.top"),sQuery(id+"F107.wireOp",EDGE,"E287.left"),sQuery(id+"F107.wireOp",EDGE,"E287.right")])],"isStart":false});
            var sketch = newSketch(context, id + "F109", { "sketchPlane" : qUnion([Q0])});
            skCircle(sketch, "E288.cCircle", {"center": v(-52.4, -39) * mm, "radius": 4.05 * mm, "construction": true});
            skLineSegment(sketch, "E288.0", {"start": v(-54.74, -34.95) * mm, "end": v(-50.07, -34.95) * mm});
            skLineSegment(sketch, "E288.1", {"start": v(-50.07, -34.95) * mm, "end": v(-47.73, -39) * mm});
            skLineSegment(sketch, "E288.2", {"start": v(-47.73, -39) * mm, "end": v(-50.07, -43.05) * mm});
            skLineSegment(sketch, "E288.3", {"start": v(-50.07, -43.05) * mm, "end": v(-54.74, -43.05) * mm});
            skLineSegment(sketch, "E288.4", {"start": v(-54.74, -43.05) * mm, "end": v(-57.08, -39) * mm});
            skLineSegment(sketch, "E288.5", {"start": v(-57.08, -39) * mm, "end": v(-54.74, -34.95) * mm});
            skPoint(sketch, "E288.0.midPoint", {"position": v(-52.4, -34.95) * mm});
            skPoint(sketch, "E289", {"position": v(-52.4, -26) * mm});
            skSolve(sketch);
        }
        {
            var Q0;
            Q0 = qSketchRegion(id + "F109", true);
            extrude(context, id + "F110", {"entities" : qUnion([Q0]), "operationType" : NewBodyOperationType.REMOVE, "oppositeDirection" : true, "depth" : getVariable(context, 'M5HexNutDepth'), "offsetDistance" : 25 * mm});
        }
        {
            var Q0;
            Q0=sQuery(id+"F109.wireOp",VERTEX,"E288.cCircle.center");
            var Q1;
            Q1=makeQuery(id+"F106.opExtrude","SWEPT_BODY",BODY,{"disambiguationData":[OSD([sQuery(id+"F105.wireOp",EDGE,"E286.bottom"),sQuery(id+"F105.wireOp",EDGE,"E286.top"),sQuery(id+"F105.wireOp",EDGE,"E286.left"),sQuery(id+"F105.wireOp",EDGE,"E286.right")])]});
            hole(context, id + "F111", {"style" : HoleStyle.SIMPLE, "endStyle" : HoleEndStyle.THROUGH, "holeDiameter" : getVariable(context, 'M5HoleDiameter'), "majorDiameter" : 5 * mm, "isTappedThrough" : true, "tappedDepth" : 12 * mm, "tapClearance" : 3, "locations" : qUnion([Q0]), "scope" : qUnion([Q1])});
        }
        {
            var Q0;
            Q0=makeQuery(id+"F108.opExtrude","SWEPT_EDGE",EDGE,{"disambiguationData":[OSD([sQuery(id+"F107.wireOp",EDGE,"E287.top"),sQuery(id+"F107.wireOp",EDGE,"E287.left")])]});
            var Q1;
            Q1=makeQuery(id+"F108.opExtrude","SWEPT_EDGE",EDGE,{"disambiguationData":[OSD([sQuery(id+"F107.wireOp",EDGE,"E287.top"),sQuery(id+"F107.wireOp",EDGE,"E287.right")])]});
            chamfer(context, id + "F112", {"entities" : qUnion([Q0, Q1]), "width" : 5 * mm, "tangentPropagation" : true});
        }
        {
            var Q0;
            {var subQ0=sQuery(id+"F107.wireOp",EDGE,"E287.top");Q0=makeQuery(id+"F112.opChamfer","BLEND_EDGE",EDGE,{"blendedFrom":[makeQuery(id+"F108.opExtrude","SWEPT_EDGE",EDGE,{"disambiguationData":[OSD([subQ0,sQuery(id+"F107.wireOp",EDGE,"E287.left")])]}),makeQuery(id+"F108.opExtrude","SWEPT_FACE",FACE,{"disambiguationData":[OSD([subQ0])]})],"blendedInto":[makeQuery(id+"F108.opExtrude","SWEPT_FACE",FACE,{"disambiguationData":[OSD([subQ0])]})]});}
            var Q1;
            {var subQ0=sQuery(id+"F107.wireOp",EDGE,"E287.left");Q1=makeQuery(id+"F112.opChamfer","BLEND_EDGE",EDGE,{"blendedFrom":[makeQuery(id+"F108.opExtrude","SWEPT_EDGE",EDGE,{"disambiguationData":[OSD([sQuery(id+"F107.wireOp",EDGE,"E287.top"),subQ0])]}),makeQuery(id+"F108.boolean.opBoolean","MERGE",FACE,{"derivedFrom":[makeQuery(id+"F106.opExtrude","SWEPT_FACE",FACE,{"disambiguationData":[OSD([sQuery(id+"F105.wireOp",EDGE,"E286.left")])]}),makeQuery(id+"F108.opExtrude","SWEPT_FACE",FACE,{"disambiguationData":[OSD([subQ0])]})]})],"blendedInto":[makeQuery(id+"F108.boolean.opBoolean","MERGE",FACE,{"derivedFrom":[makeQuery(id+"F106.opExtrude","SWEPT_FACE",FACE,{"disambiguationData":[OSD([sQuery(id+"F105.wireOp",EDGE,"E286.left")])]}),makeQuery(id+"F108.opExtrude","SWEPT_FACE",FACE,{"disambiguationData":[OSD([subQ0])]})]})]});}
            var Q2;
            {var subQ0=sQuery(id+"F107.wireOp",EDGE,"E287.top");Q2=makeQuery(id+"F112.opChamfer","BLEND_EDGE",EDGE,{"blendedFrom":[makeQuery(id+"F108.opExtrude","SWEPT_EDGE",EDGE,{"disambiguationData":[OSD([subQ0,sQuery(id+"F107.wireOp",EDGE,"E287.right")])]}),makeQuery(id+"F108.opExtrude","SWEPT_FACE",FACE,{"disambiguationData":[OSD([subQ0])]})],"blendedInto":[makeQuery(id+"F108.opExtrude","SWEPT_FACE",FACE,{"disambiguationData":[OSD([subQ0])]})]});}
            var Q3;
            {var subQ0=sQuery(id+"F107.wireOp",EDGE,"E287.right");Q3=makeQuery(id+"F112.opChamfer","BLEND_EDGE",EDGE,{"blendedFrom":[makeQuery(id+"F108.opExtrude","SWEPT_EDGE",EDGE,{"disambiguationData":[OSD([sQuery(id+"F107.wireOp",EDGE,"E287.top"),subQ0])]}),makeQuery(id+"F108.boolean.opBoolean","MERGE",FACE,{"derivedFrom":[makeQuery(id+"F106.opExtrude","SWEPT_FACE",FACE,{"disambiguationData":[OSD([sQuery(id+"F105.wireOp",EDGE,"E286.right")])]}),makeQuery(id+"F108.opExtrude","SWEPT_FACE",FACE,{"disambiguationData":[OSD([subQ0])]})]})],"blendedInto":[makeQuery(id+"F108.boolean.opBoolean","MERGE",FACE,{"derivedFrom":[makeQuery(id+"F106.opExtrude","SWEPT_FACE",FACE,{"disambiguationData":[OSD([sQuery(id+"F105.wireOp",EDGE,"E286.right")])]}),makeQuery(id+"F108.opExtrude","SWEPT_FACE",FACE,{"disambiguationData":[OSD([subQ0])]})]})]});}
            var Q4;
            {var subQ0=sQuery(id+"F107.wireOp",EDGE,"E287.right");Q4=makeQuery(id+"F112.opChamfer","BLEND_EDGE",EDGE,{"blendedFrom":[makeQuery(id+"F108.opExtrude","SWEPT_EDGE",EDGE,{"disambiguationData":[OSD([sQuery(id+"F107.wireOp",EDGE,"E287.top"),subQ0])]}),makeQuery(id+"F108.opExtrude","SWEPT_FACE",FACE,{"disambiguationData":[OSD([subQ0])]})],"blendedInto":[makeQuery(id+"F108.opExtrude","SWEPT_FACE",FACE,{"disambiguationData":[OSD([subQ0])]})]});}
            fillet(context, id + "F113", {"entities" : qUnion([Q0, Q1, Q2, Q3, Q4]), "radius" : getVariable(context, 'FilletRadius'), "tangentPropagation" : true, "allowEdgeOverflow" : false});
        }
        {
            var Q0;
            Q0 = qSketchRegion(id + "F38", true);
            extrude(context, id + "F114", {"entities" : qUnion([Q0]), "operationType" : NewBodyOperationType.REMOVE, "depth" : 25 * mm, "offsetDistance" : 25 * mm});
        }
        {
            var Q0;
            Q0 = qSketchRegion(id + "F84", true);
            extrude(context, id + "F115", {"entities" : qUnion([Q0]), "operationType" : NewBodyOperationType.REMOVE, "oppositeDirection" : true, "depth" : 25 * mm, "offsetDistance" : 25 * mm});
        }
    });
